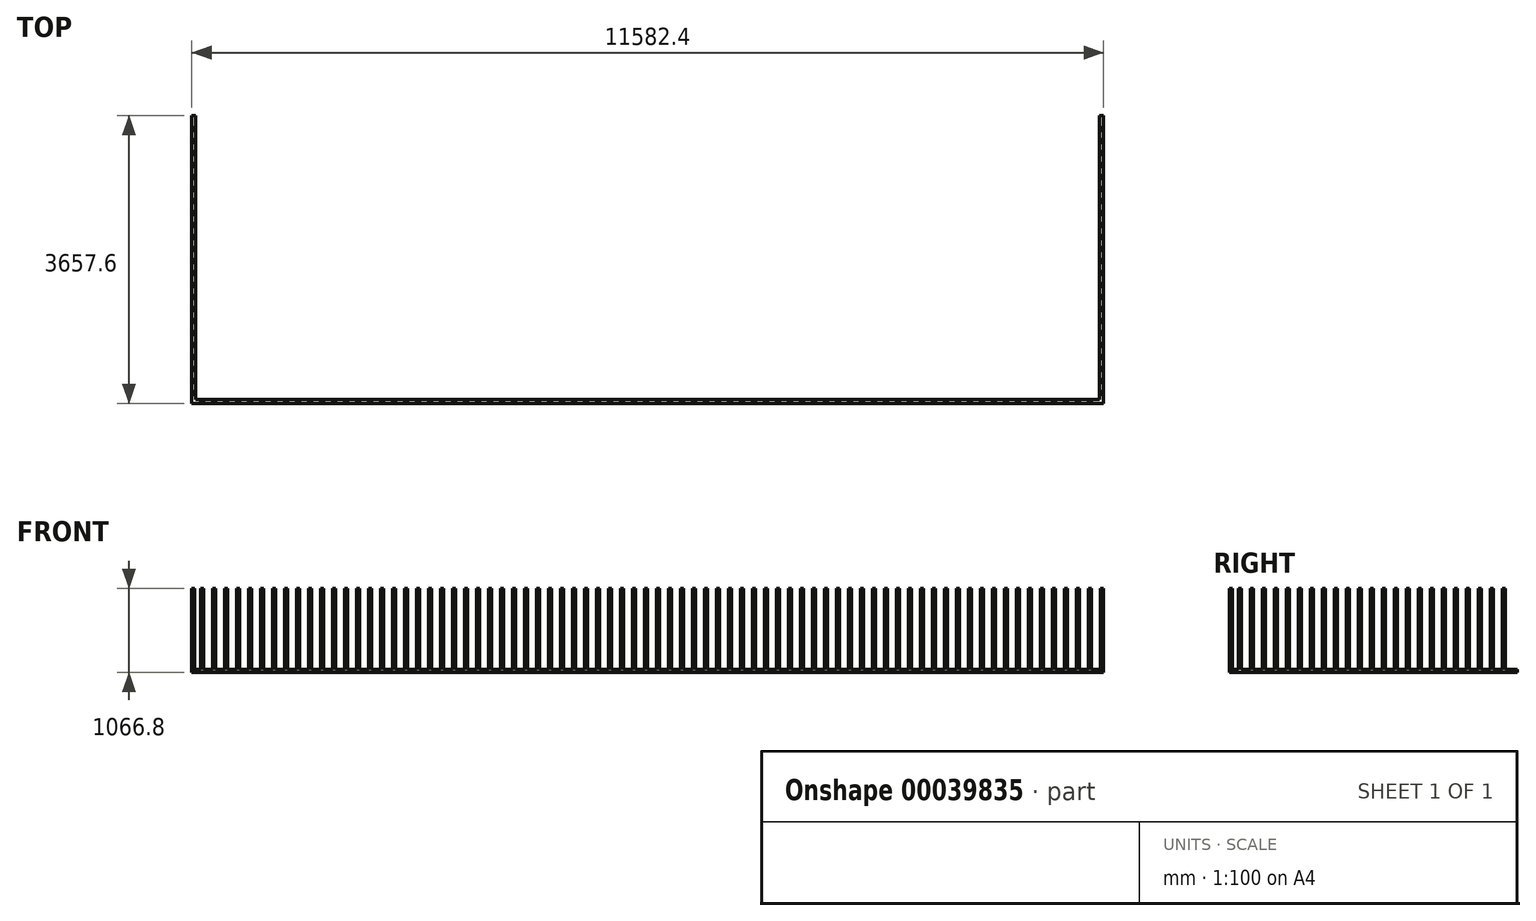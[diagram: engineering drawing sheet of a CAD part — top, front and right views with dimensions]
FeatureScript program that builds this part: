
annotation { "Feature Type Name" : "Feature", "Feature Type Description" : "" }
export const myFeature = defineFeature(function(context is Context, id is Id, definition is map)
    precondition{}
    {
        {
            var Q0;
            Q0=qCreatedBy(makeId("Top.planeOp"),FACE);
            var sketch = newSketch(context, id + "F0", { "sketchPlane" : qUnion([Q0])});
            skLineSegment(sketch, "E0", {"start": v(-11531.6, 0) * mm, "end": v(-11531.6, -3657.6) * mm});
            skLineSegment(sketch, "E1", {"start": v(-11531.6, -3657.6) * mm, "end": v(50.8, -3657.6) * mm});
            skLineSegment(sketch, "E2", {"start": v(50.8, -3657.6) * mm, "end": v(50.8, 0) * mm});
            skLineSegment(sketch, "E3", {"start": v(50.8, 0) * mm, "end": v(0, 0) * mm});
            skLineSegment(sketch, "E4", {"start": v(0, 0) * mm, "end": v(0, -3606.8) * mm});
            skLineSegment(sketch, "E5", {"start": v(0, -3606.8) * mm, "end": v(-11480.8, -3606.8) * mm});
            skLineSegment(sketch, "E6", {"start": v(-11480.8, -3606.8) * mm, "end": v(-11480.8, 0) * mm});
            skLineSegment(sketch, "E7", {"start": v(-11480.8, 0) * mm, "end": v(-11531.6, 0) * mm});
            skLineSegment(sketch, "E8.bottom", {"start": v(50.8, 0) * mm, "end": v(12.7, 0) * mm});
            skLineSegment(sketch, "E8.top", {"start": v(50.8, -38.1) * mm, "end": v(12.7, -38.1) * mm});
            skLineSegment(sketch, "E8.left", {"start": v(50.8, 0) * mm, "end": v(50.8, -38.1) * mm});
            skLineSegment(sketch, "E8.right", {"start": v(12.7, 0) * mm, "end": v(12.7, -38.1) * mm});
            skLineSegment(sketch, "E9.0.1.0", {"start": v(50.8, -190.5) * mm, "end": v(12.7, -190.5) * mm});
            skLineSegment(sketch, "E9.0.1.1", {"start": v(50.8, -152.4) * mm, "end": v(12.7, -152.4) * mm});
            skLineSegment(sketch, "E9.0.1.2", {"start": v(12.7, -152.4) * mm, "end": v(12.7, -190.5) * mm});
            skLineSegment(sketch, "E9.0.2.0", {"start": v(50.8, -342.9) * mm, "end": v(12.7, -342.9) * mm});
            skLineSegment(sketch, "E9.0.2.1", {"start": v(50.8, -304.8) * mm, "end": v(12.7, -304.8) * mm});
            skLineSegment(sketch, "E9.0.2.2", {"start": v(12.7, -304.8) * mm, "end": v(12.7, -342.9) * mm});
            skLineSegment(sketch, "E9.0.3.0", {"start": v(50.8, -495.3) * mm, "end": v(12.7, -495.3) * mm});
            skLineSegment(sketch, "E9.0.3.1", {"start": v(50.8, -457.2) * mm, "end": v(12.7, -457.2) * mm});
            skLineSegment(sketch, "E9.0.3.2", {"start": v(12.7, -457.2) * mm, "end": v(12.7, -495.3) * mm});
            skLineSegment(sketch, "E9.0.4.0", {"start": v(50.8, -647.7) * mm, "end": v(12.7, -647.7) * mm});
            skLineSegment(sketch, "E9.0.4.1", {"start": v(50.8, -609.6) * mm, "end": v(12.7, -609.6) * mm});
            skLineSegment(sketch, "E9.0.4.2", {"start": v(12.7, -609.6) * mm, "end": v(12.7, -647.7) * mm});
            skLineSegment(sketch, "E9.0.5.0", {"start": v(50.8, -800.1) * mm, "end": v(12.7, -800.1) * mm});
            skLineSegment(sketch, "E9.0.5.1", {"start": v(50.8, -762) * mm, "end": v(12.7, -762) * mm});
            skLineSegment(sketch, "E9.0.5.2", {"start": v(12.7, -762) * mm, "end": v(12.7, -800.1) * mm});
            skLineSegment(sketch, "E9.0.6.0", {"start": v(50.8, -952.5) * mm, "end": v(12.7, -952.5) * mm});
            skLineSegment(sketch, "E9.0.6.1", {"start": v(50.8, -914.4) * mm, "end": v(12.7, -914.4) * mm});
            skLineSegment(sketch, "E9.0.6.2", {"start": v(12.7, -914.4) * mm, "end": v(12.7, -952.5) * mm});
            skLineSegment(sketch, "E9.0.7.0", {"start": v(50.8, -1104.9) * mm, "end": v(12.7, -1104.9) * mm});
            skLineSegment(sketch, "E9.0.7.1", {"start": v(50.8, -1066.8) * mm, "end": v(12.7, -1066.8) * mm});
            skLineSegment(sketch, "E9.0.7.2", {"start": v(12.7, -1066.8) * mm, "end": v(12.7, -1104.9) * mm});
            skLineSegment(sketch, "E9.0.8.0", {"start": v(50.8, -1257.3) * mm, "end": v(12.7, -1257.3) * mm});
            skLineSegment(sketch, "E9.0.8.1", {"start": v(50.8, -1219.2) * mm, "end": v(12.7, -1219.2) * mm});
            skLineSegment(sketch, "E9.0.8.2", {"start": v(12.7, -1219.2) * mm, "end": v(12.7, -1257.3) * mm});
            skLineSegment(sketch, "E9.0.9.0", {"start": v(50.8, -1409.7) * mm, "end": v(12.7, -1409.7) * mm});
            skLineSegment(sketch, "E9.0.9.1", {"start": v(50.8, -1371.6) * mm, "end": v(12.7, -1371.6) * mm});
            skLineSegment(sketch, "E9.0.9.2", {"start": v(12.7, -1371.6) * mm, "end": v(12.7, -1409.7) * mm});
            skLineSegment(sketch, "E9.0.10.0", {"start": v(50.8, -1562.1) * mm, "end": v(12.7, -1562.1) * mm});
            skLineSegment(sketch, "E9.0.10.1", {"start": v(50.8, -1524) * mm, "end": v(12.7, -1524) * mm});
            skLineSegment(sketch, "E9.0.10.2", {"start": v(12.7, -1524) * mm, "end": v(12.7, -1562.1) * mm});
            skLineSegment(sketch, "E9.0.11.0", {"start": v(50.8, -1714.5) * mm, "end": v(12.7, -1714.5) * mm});
            skLineSegment(sketch, "E9.0.11.1", {"start": v(50.8, -1676.4) * mm, "end": v(12.7, -1676.4) * mm});
            skLineSegment(sketch, "E9.0.11.2", {"start": v(12.7, -1676.4) * mm, "end": v(12.7, -1714.5) * mm});
            skLineSegment(sketch, "E9.0.12.0", {"start": v(50.8, -1866.9) * mm, "end": v(12.7, -1866.9) * mm});
            skLineSegment(sketch, "E9.0.12.1", {"start": v(50.8, -1828.8) * mm, "end": v(12.7, -1828.8) * mm});
            skLineSegment(sketch, "E9.0.12.2", {"start": v(12.7, -1828.8) * mm, "end": v(12.7, -1866.9) * mm});
            skLineSegment(sketch, "E9.0.13.0", {"start": v(50.8, -2019.3) * mm, "end": v(12.7, -2019.3) * mm});
            skLineSegment(sketch, "E9.0.13.1", {"start": v(50.8, -1981.2) * mm, "end": v(12.7, -1981.2) * mm});
            skLineSegment(sketch, "E9.0.13.2", {"start": v(12.7, -1981.2) * mm, "end": v(12.7, -2019.3) * mm});
            skLineSegment(sketch, "E9.0.14.0", {"start": v(50.8, -2171.7) * mm, "end": v(12.7, -2171.7) * mm});
            skLineSegment(sketch, "E9.0.14.1", {"start": v(50.8, -2133.6) * mm, "end": v(12.7, -2133.6) * mm});
            skLineSegment(sketch, "E9.0.14.2", {"start": v(12.7, -2133.6) * mm, "end": v(12.7, -2171.7) * mm});
            skLineSegment(sketch, "E9.0.15.0", {"start": v(50.8, -2324.1) * mm, "end": v(12.7, -2324.1) * mm});
            skLineSegment(sketch, "E9.0.15.1", {"start": v(50.8, -2286) * mm, "end": v(12.7, -2286) * mm});
            skLineSegment(sketch, "E9.0.15.2", {"start": v(12.7, -2286) * mm, "end": v(12.7, -2324.1) * mm});
            skLineSegment(sketch, "E9.0.16.0", {"start": v(50.8, -2476.5) * mm, "end": v(12.7, -2476.5) * mm});
            skLineSegment(sketch, "E9.0.16.1", {"start": v(50.8, -2438.4) * mm, "end": v(12.7, -2438.4) * mm});
            skLineSegment(sketch, "E9.0.16.2", {"start": v(12.7, -2438.4) * mm, "end": v(12.7, -2476.5) * mm});
            skLineSegment(sketch, "E9.0.17.0", {"start": v(50.8, -2628.9) * mm, "end": v(12.7, -2628.9) * mm});
            skLineSegment(sketch, "E9.0.17.1", {"start": v(50.8, -2590.8) * mm, "end": v(12.7, -2590.8) * mm});
            skLineSegment(sketch, "E9.0.17.2", {"start": v(12.7, -2590.8) * mm, "end": v(12.7, -2628.9) * mm});
            skLineSegment(sketch, "E9.0.18.0", {"start": v(50.8, -2781.3) * mm, "end": v(12.7, -2781.3) * mm});
            skLineSegment(sketch, "E9.0.18.1", {"start": v(50.8, -2743.2) * mm, "end": v(12.7, -2743.2) * mm});
            skLineSegment(sketch, "E9.0.18.2", {"start": v(12.7, -2743.2) * mm, "end": v(12.7, -2781.3) * mm});
            skLineSegment(sketch, "E9.0.19.0", {"start": v(50.8, -2933.7) * mm, "end": v(12.7, -2933.7) * mm});
            skLineSegment(sketch, "E9.0.19.1", {"start": v(50.8, -2895.6) * mm, "end": v(12.7, -2895.6) * mm});
            skLineSegment(sketch, "E9.0.19.2", {"start": v(12.7, -2895.6) * mm, "end": v(12.7, -2933.7) * mm});
            skLineSegment(sketch, "E9.0.20.0", {"start": v(50.8, -3086.1) * mm, "end": v(12.7, -3086.1) * mm});
            skLineSegment(sketch, "E9.0.20.1", {"start": v(50.8, -3048) * mm, "end": v(12.7, -3048) * mm});
            skLineSegment(sketch, "E9.0.20.2", {"start": v(12.7, -3048) * mm, "end": v(12.7, -3086.1) * mm});
            skLineSegment(sketch, "E9.0.21.0", {"start": v(50.8, -3238.5) * mm, "end": v(12.7, -3238.5) * mm});
            skLineSegment(sketch, "E9.0.21.1", {"start": v(50.8, -3200.4) * mm, "end": v(12.7, -3200.4) * mm});
            skLineSegment(sketch, "E9.0.21.2", {"start": v(12.7, -3200.4) * mm, "end": v(12.7, -3238.5) * mm});
            skLineSegment(sketch, "E9.0.22.0", {"start": v(50.8, -3390.9) * mm, "end": v(12.7, -3390.9) * mm});
            skLineSegment(sketch, "E9.0.22.1", {"start": v(50.8, -3352.8) * mm, "end": v(12.7, -3352.8) * mm});
            skLineSegment(sketch, "E9.0.22.2", {"start": v(12.7, -3352.8) * mm, "end": v(12.7, -3390.9) * mm});
            skLineSegment(sketch, "E9.0.23.0", {"start": v(50.8, -3543.3) * mm, "end": v(12.7, -3543.3) * mm});
            skLineSegment(sketch, "E9.0.23.1", {"start": v(50.8, -3505.2) * mm, "end": v(12.7, -3505.2) * mm});
            skLineSegment(sketch, "E9.0.23.2", {"start": v(12.7, -3505.2) * mm, "end": v(12.7, -3543.3) * mm});
            skLineSegment(sketch, "E9.direction1", {"start": v(12.7, -38.1) * mm, "end": v(-12.7, -38.1) * mm, "construction": true});
            skLineSegment(sketch, "E9.direction2", {"start": v(12.7, -38.1) * mm, "end": v(12.7, -190.5) * mm, "construction": true});
            skLineSegment(sketch, "E10.bottom", {"start": v(50.8, -3657.6) * mm, "end": v(12.7, -3657.6) * mm});
            skLineSegment(sketch, "E10.top", {"start": v(50.8, -3619.5) * mm, "end": v(12.7, -3619.5) * mm});
            skLineSegment(sketch, "E10.left", {"start": v(50.8, -3657.6) * mm, "end": v(50.8, -3619.5) * mm});
            skLineSegment(sketch, "E10.right", {"start": v(12.7, -3657.6) * mm, "end": v(12.7, -3619.5) * mm});
            skLineSegment(sketch, "E11.1.0.0", {"start": v(-139.7, -3657.6) * mm, "end": v(-139.7, -3619.5) * mm});
            skLineSegment(sketch, "E11.1.0.1", {"start": v(-101.6, -3657.6) * mm, "end": v(-101.6, -3619.5) * mm});
            skLineSegment(sketch, "E11.1.0.2", {"start": v(-101.6, -3619.5) * mm, "end": v(-139.7, -3619.5) * mm});
            skLineSegment(sketch, "E11.1.0.3", {"start": v(-101.6, -3657.6) * mm, "end": v(-139.7, -3657.6) * mm});
            skLineSegment(sketch, "E11.2.0.0", {"start": v(-292.1, -3657.6) * mm, "end": v(-292.1, -3619.5) * mm});
            skLineSegment(sketch, "E11.2.0.1", {"start": v(-254, -3657.6) * mm, "end": v(-254, -3619.5) * mm});
            skLineSegment(sketch, "E11.2.0.2", {"start": v(-254, -3619.5) * mm, "end": v(-292.1, -3619.5) * mm});
            skLineSegment(sketch, "E11.2.0.3", {"start": v(-254, -3657.6) * mm, "end": v(-292.1, -3657.6) * mm});
            skLineSegment(sketch, "E11.3.0.0", {"start": v(-444.5, -3657.6) * mm, "end": v(-444.5, -3619.5) * mm});
            skLineSegment(sketch, "E11.3.0.1", {"start": v(-406.4, -3657.6) * mm, "end": v(-406.4, -3619.5) * mm});
            skLineSegment(sketch, "E11.3.0.2", {"start": v(-406.4, -3619.5) * mm, "end": v(-444.5, -3619.5) * mm});
            skLineSegment(sketch, "E11.3.0.3", {"start": v(-406.4, -3657.6) * mm, "end": v(-444.5, -3657.6) * mm});
            skLineSegment(sketch, "E11.4.0.0", {"start": v(-596.9, -3657.6) * mm, "end": v(-596.9, -3619.5) * mm});
            skLineSegment(sketch, "E11.4.0.1", {"start": v(-558.8, -3657.6) * mm, "end": v(-558.8, -3619.5) * mm});
            skLineSegment(sketch, "E11.4.0.2", {"start": v(-558.8, -3619.5) * mm, "end": v(-596.9, -3619.5) * mm});
            skLineSegment(sketch, "E11.4.0.3", {"start": v(-558.8, -3657.6) * mm, "end": v(-596.9, -3657.6) * mm});
            skLineSegment(sketch, "E11.5.0.0", {"start": v(-749.3, -3657.6) * mm, "end": v(-749.3, -3619.5) * mm});
            skLineSegment(sketch, "E11.5.0.1", {"start": v(-711.2, -3657.6) * mm, "end": v(-711.2, -3619.5) * mm});
            skLineSegment(sketch, "E11.5.0.2", {"start": v(-711.2, -3619.5) * mm, "end": v(-749.3, -3619.5) * mm});
            skLineSegment(sketch, "E11.5.0.3", {"start": v(-711.2, -3657.6) * mm, "end": v(-749.3, -3657.6) * mm});
            skLineSegment(sketch, "E11.6.0.0", {"start": v(-901.7, -3657.6) * mm, "end": v(-901.7, -3619.5) * mm});
            skLineSegment(sketch, "E11.6.0.1", {"start": v(-863.6, -3657.6) * mm, "end": v(-863.6, -3619.5) * mm});
            skLineSegment(sketch, "E11.6.0.2", {"start": v(-863.6, -3619.5) * mm, "end": v(-901.7, -3619.5) * mm});
            skLineSegment(sketch, "E11.6.0.3", {"start": v(-863.6, -3657.6) * mm, "end": v(-901.7, -3657.6) * mm});
            skLineSegment(sketch, "E11.7.0.0", {"start": v(-1054.1, -3657.6) * mm, "end": v(-1054.1, -3619.5) * mm});
            skLineSegment(sketch, "E11.7.0.1", {"start": v(-1016, -3657.6) * mm, "end": v(-1016, -3619.5) * mm});
            skLineSegment(sketch, "E11.7.0.2", {"start": v(-1016, -3619.5) * mm, "end": v(-1054.1, -3619.5) * mm});
            skLineSegment(sketch, "E11.7.0.3", {"start": v(-1016, -3657.6) * mm, "end": v(-1054.1, -3657.6) * mm});
            skLineSegment(sketch, "E11.8.0.0", {"start": v(-1206.5, -3657.6) * mm, "end": v(-1206.5, -3619.5) * mm});
            skLineSegment(sketch, "E11.8.0.1", {"start": v(-1168.4, -3657.6) * mm, "end": v(-1168.4, -3619.5) * mm});
            skLineSegment(sketch, "E11.8.0.2", {"start": v(-1168.4, -3619.5) * mm, "end": v(-1206.5, -3619.5) * mm});
            skLineSegment(sketch, "E11.8.0.3", {"start": v(-1168.4, -3657.6) * mm, "end": v(-1206.5, -3657.6) * mm});
            skLineSegment(sketch, "E11.9.0.0", {"start": v(-1358.9, -3657.6) * mm, "end": v(-1358.9, -3619.5) * mm});
            skLineSegment(sketch, "E11.9.0.1", {"start": v(-1320.8, -3657.6) * mm, "end": v(-1320.8, -3619.5) * mm});
            skLineSegment(sketch, "E11.9.0.2", {"start": v(-1320.8, -3619.5) * mm, "end": v(-1358.9, -3619.5) * mm});
            skLineSegment(sketch, "E11.9.0.3", {"start": v(-1320.8, -3657.6) * mm, "end": v(-1358.9, -3657.6) * mm});
            skLineSegment(sketch, "E11.10.0.0", {"start": v(-1511.3, -3657.6) * mm, "end": v(-1511.3, -3619.5) * mm});
            skLineSegment(sketch, "E11.10.0.1", {"start": v(-1473.2, -3657.6) * mm, "end": v(-1473.2, -3619.5) * mm});
            skLineSegment(sketch, "E11.10.0.2", {"start": v(-1473.2, -3619.5) * mm, "end": v(-1511.3, -3619.5) * mm});
            skLineSegment(sketch, "E11.10.0.3", {"start": v(-1473.2, -3657.6) * mm, "end": v(-1511.3, -3657.6) * mm});
            skLineSegment(sketch, "E11.11.0.0", {"start": v(-1663.7, -3657.6) * mm, "end": v(-1663.7, -3619.5) * mm});
            skLineSegment(sketch, "E11.11.0.1", {"start": v(-1625.6, -3657.6) * mm, "end": v(-1625.6, -3619.5) * mm});
            skLineSegment(sketch, "E11.11.0.2", {"start": v(-1625.6, -3619.5) * mm, "end": v(-1663.7, -3619.5) * mm});
            skLineSegment(sketch, "E11.11.0.3", {"start": v(-1625.6, -3657.6) * mm, "end": v(-1663.7, -3657.6) * mm});
            skLineSegment(sketch, "E11.12.0.0", {"start": v(-1816.1, -3657.6) * mm, "end": v(-1816.1, -3619.5) * mm});
            skLineSegment(sketch, "E11.12.0.1", {"start": v(-1778, -3657.6) * mm, "end": v(-1778, -3619.5) * mm});
            skLineSegment(sketch, "E11.12.0.2", {"start": v(-1778, -3619.5) * mm, "end": v(-1816.1, -3619.5) * mm});
            skLineSegment(sketch, "E11.12.0.3", {"start": v(-1778, -3657.6) * mm, "end": v(-1816.1, -3657.6) * mm});
            skLineSegment(sketch, "E11.13.0.0", {"start": v(-1968.5, -3657.6) * mm, "end": v(-1968.5, -3619.5) * mm});
            skLineSegment(sketch, "E11.13.0.1", {"start": v(-1930.4, -3657.6) * mm, "end": v(-1930.4, -3619.5) * mm});
            skLineSegment(sketch, "E11.13.0.2", {"start": v(-1930.4, -3619.5) * mm, "end": v(-1968.5, -3619.5) * mm});
            skLineSegment(sketch, "E11.13.0.3", {"start": v(-1930.4, -3657.6) * mm, "end": v(-1968.5, -3657.6) * mm});
            skLineSegment(sketch, "E11.14.0.0", {"start": v(-2120.9, -3657.6) * mm, "end": v(-2120.9, -3619.5) * mm});
            skLineSegment(sketch, "E11.14.0.1", {"start": v(-2082.8, -3657.6) * mm, "end": v(-2082.8, -3619.5) * mm});
            skLineSegment(sketch, "E11.14.0.2", {"start": v(-2082.8, -3619.5) * mm, "end": v(-2120.9, -3619.5) * mm});
            skLineSegment(sketch, "E11.14.0.3", {"start": v(-2082.8, -3657.6) * mm, "end": v(-2120.9, -3657.6) * mm});
            skLineSegment(sketch, "E11.15.0.0", {"start": v(-2273.3, -3657.6) * mm, "end": v(-2273.3, -3619.5) * mm});
            skLineSegment(sketch, "E11.15.0.1", {"start": v(-2235.2, -3657.6) * mm, "end": v(-2235.2, -3619.5) * mm});
            skLineSegment(sketch, "E11.15.0.2", {"start": v(-2235.2, -3619.5) * mm, "end": v(-2273.3, -3619.5) * mm});
            skLineSegment(sketch, "E11.15.0.3", {"start": v(-2235.2, -3657.6) * mm, "end": v(-2273.3, -3657.6) * mm});
            skLineSegment(sketch, "E11.16.0.0", {"start": v(-2425.7, -3657.6) * mm, "end": v(-2425.7, -3619.5) * mm});
            skLineSegment(sketch, "E11.16.0.1", {"start": v(-2387.6, -3657.6) * mm, "end": v(-2387.6, -3619.5) * mm});
            skLineSegment(sketch, "E11.16.0.2", {"start": v(-2387.6, -3619.5) * mm, "end": v(-2425.7, -3619.5) * mm});
            skLineSegment(sketch, "E11.16.0.3", {"start": v(-2387.6, -3657.6) * mm, "end": v(-2425.7, -3657.6) * mm});
            skLineSegment(sketch, "E11.17.0.0", {"start": v(-2578.1, -3657.6) * mm, "end": v(-2578.1, -3619.5) * mm});
            skLineSegment(sketch, "E11.17.0.1", {"start": v(-2540, -3657.6) * mm, "end": v(-2540, -3619.5) * mm});
            skLineSegment(sketch, "E11.17.0.2", {"start": v(-2540, -3619.5) * mm, "end": v(-2578.1, -3619.5) * mm});
            skLineSegment(sketch, "E11.17.0.3", {"start": v(-2540, -3657.6) * mm, "end": v(-2578.1, -3657.6) * mm});
            skLineSegment(sketch, "E11.18.0.0", {"start": v(-2730.5, -3657.6) * mm, "end": v(-2730.5, -3619.5) * mm});
            skLineSegment(sketch, "E11.18.0.1", {"start": v(-2692.4, -3657.6) * mm, "end": v(-2692.4, -3619.5) * mm});
            skLineSegment(sketch, "E11.18.0.2", {"start": v(-2692.4, -3619.5) * mm, "end": v(-2730.5, -3619.5) * mm});
            skLineSegment(sketch, "E11.18.0.3", {"start": v(-2692.4, -3657.6) * mm, "end": v(-2730.5, -3657.6) * mm});
            skLineSegment(sketch, "E11.19.0.0", {"start": v(-2882.9, -3657.6) * mm, "end": v(-2882.9, -3619.5) * mm});
            skLineSegment(sketch, "E11.19.0.1", {"start": v(-2844.8, -3657.6) * mm, "end": v(-2844.8, -3619.5) * mm});
            skLineSegment(sketch, "E11.19.0.2", {"start": v(-2844.8, -3619.5) * mm, "end": v(-2882.9, -3619.5) * mm});
            skLineSegment(sketch, "E11.19.0.3", {"start": v(-2844.8, -3657.6) * mm, "end": v(-2882.9, -3657.6) * mm});
            skLineSegment(sketch, "E11.20.0.0", {"start": v(-3035.3, -3657.6) * mm, "end": v(-3035.3, -3619.5) * mm});
            skLineSegment(sketch, "E11.20.0.1", {"start": v(-2997.2, -3657.6) * mm, "end": v(-2997.2, -3619.5) * mm});
            skLineSegment(sketch, "E11.20.0.2", {"start": v(-2997.2, -3619.5) * mm, "end": v(-3035.3, -3619.5) * mm});
            skLineSegment(sketch, "E11.20.0.3", {"start": v(-2997.2, -3657.6) * mm, "end": v(-3035.3, -3657.6) * mm});
            skLineSegment(sketch, "E11.21.0.0", {"start": v(-3187.7, -3657.6) * mm, "end": v(-3187.7, -3619.5) * mm});
            skLineSegment(sketch, "E11.21.0.1", {"start": v(-3149.6, -3657.6) * mm, "end": v(-3149.6, -3619.5) * mm});
            skLineSegment(sketch, "E11.21.0.2", {"start": v(-3149.6, -3619.5) * mm, "end": v(-3187.7, -3619.5) * mm});
            skLineSegment(sketch, "E11.21.0.3", {"start": v(-3149.6, -3657.6) * mm, "end": v(-3187.7, -3657.6) * mm});
            skLineSegment(sketch, "E11.22.0.0", {"start": v(-3340.1, -3657.6) * mm, "end": v(-3340.1, -3619.5) * mm});
            skLineSegment(sketch, "E11.22.0.1", {"start": v(-3302, -3657.6) * mm, "end": v(-3302, -3619.5) * mm});
            skLineSegment(sketch, "E11.22.0.2", {"start": v(-3302, -3619.5) * mm, "end": v(-3340.1, -3619.5) * mm});
            skLineSegment(sketch, "E11.22.0.3", {"start": v(-3302, -3657.6) * mm, "end": v(-3340.1, -3657.6) * mm});
            skLineSegment(sketch, "E11.23.0.0", {"start": v(-3492.5, -3657.6) * mm, "end": v(-3492.5, -3619.5) * mm});
            skLineSegment(sketch, "E11.23.0.1", {"start": v(-3454.4, -3657.6) * mm, "end": v(-3454.4, -3619.5) * mm});
            skLineSegment(sketch, "E11.23.0.2", {"start": v(-3454.4, -3619.5) * mm, "end": v(-3492.5, -3619.5) * mm});
            skLineSegment(sketch, "E11.23.0.3", {"start": v(-3454.4, -3657.6) * mm, "end": v(-3492.5, -3657.6) * mm});
            skLineSegment(sketch, "E11.24.0.0", {"start": v(-3644.9, -3657.6) * mm, "end": v(-3644.9, -3619.5) * mm});
            skLineSegment(sketch, "E11.24.0.1", {"start": v(-3606.8, -3657.6) * mm, "end": v(-3606.8, -3619.5) * mm});
            skLineSegment(sketch, "E11.24.0.2", {"start": v(-3606.8, -3619.5) * mm, "end": v(-3644.9, -3619.5) * mm});
            skLineSegment(sketch, "E11.24.0.3", {"start": v(-3606.8, -3657.6) * mm, "end": v(-3644.9, -3657.6) * mm});
            skLineSegment(sketch, "E11.25.0.0", {"start": v(-3797.3, -3657.6) * mm, "end": v(-3797.3, -3619.5) * mm});
            skLineSegment(sketch, "E11.25.0.1", {"start": v(-3759.2, -3657.6) * mm, "end": v(-3759.2, -3619.5) * mm});
            skLineSegment(sketch, "E11.25.0.2", {"start": v(-3759.2, -3619.5) * mm, "end": v(-3797.3, -3619.5) * mm});
            skLineSegment(sketch, "E11.25.0.3", {"start": v(-3759.2, -3657.6) * mm, "end": v(-3797.3, -3657.6) * mm});
            skLineSegment(sketch, "E11.26.0.0", {"start": v(-3949.7, -3657.6) * mm, "end": v(-3949.7, -3619.5) * mm});
            skLineSegment(sketch, "E11.26.0.1", {"start": v(-3911.6, -3657.6) * mm, "end": v(-3911.6, -3619.5) * mm});
            skLineSegment(sketch, "E11.26.0.2", {"start": v(-3911.6, -3619.5) * mm, "end": v(-3949.7, -3619.5) * mm});
            skLineSegment(sketch, "E11.26.0.3", {"start": v(-3911.6, -3657.6) * mm, "end": v(-3949.7, -3657.6) * mm});
            skLineSegment(sketch, "E11.27.0.0", {"start": v(-4102.1, -3657.6) * mm, "end": v(-4102.1, -3619.5) * mm});
            skLineSegment(sketch, "E11.27.0.1", {"start": v(-4064, -3657.6) * mm, "end": v(-4064, -3619.5) * mm});
            skLineSegment(sketch, "E11.27.0.2", {"start": v(-4064, -3619.5) * mm, "end": v(-4102.1, -3619.5) * mm});
            skLineSegment(sketch, "E11.27.0.3", {"start": v(-4064, -3657.6) * mm, "end": v(-4102.1, -3657.6) * mm});
            skLineSegment(sketch, "E11.28.0.0", {"start": v(-4254.5, -3657.6) * mm, "end": v(-4254.5, -3619.5) * mm});
            skLineSegment(sketch, "E11.28.0.1", {"start": v(-4216.4, -3657.6) * mm, "end": v(-4216.4, -3619.5) * mm});
            skLineSegment(sketch, "E11.28.0.2", {"start": v(-4216.4, -3619.5) * mm, "end": v(-4254.5, -3619.5) * mm});
            skLineSegment(sketch, "E11.28.0.3", {"start": v(-4216.4, -3657.6) * mm, "end": v(-4254.5, -3657.6) * mm});
            skLineSegment(sketch, "E11.29.0.0", {"start": v(-4406.9, -3657.6) * mm, "end": v(-4406.9, -3619.5) * mm});
            skLineSegment(sketch, "E11.29.0.1", {"start": v(-4368.8, -3657.6) * mm, "end": v(-4368.8, -3619.5) * mm});
            skLineSegment(sketch, "E11.29.0.2", {"start": v(-4368.8, -3619.5) * mm, "end": v(-4406.9, -3619.5) * mm});
            skLineSegment(sketch, "E11.29.0.3", {"start": v(-4368.8, -3657.6) * mm, "end": v(-4406.9, -3657.6) * mm});
            skLineSegment(sketch, "E11.30.0.0", {"start": v(-4559.3, -3657.6) * mm, "end": v(-4559.3, -3619.5) * mm});
            skLineSegment(sketch, "E11.30.0.1", {"start": v(-4521.2, -3657.6) * mm, "end": v(-4521.2, -3619.5) * mm});
            skLineSegment(sketch, "E11.30.0.2", {"start": v(-4521.2, -3619.5) * mm, "end": v(-4559.3, -3619.5) * mm});
            skLineSegment(sketch, "E11.30.0.3", {"start": v(-4521.2, -3657.6) * mm, "end": v(-4559.3, -3657.6) * mm});
            skLineSegment(sketch, "E11.31.0.0", {"start": v(-4711.7, -3657.6) * mm, "end": v(-4711.7, -3619.5) * mm});
            skLineSegment(sketch, "E11.31.0.1", {"start": v(-4673.6, -3657.6) * mm, "end": v(-4673.6, -3619.5) * mm});
            skLineSegment(sketch, "E11.31.0.2", {"start": v(-4673.6, -3619.5) * mm, "end": v(-4711.7, -3619.5) * mm});
            skLineSegment(sketch, "E11.31.0.3", {"start": v(-4673.6, -3657.6) * mm, "end": v(-4711.7, -3657.6) * mm});
            skLineSegment(sketch, "E11.32.0.0", {"start": v(-4864.1, -3657.6) * mm, "end": v(-4864.1, -3619.5) * mm});
            skLineSegment(sketch, "E11.32.0.1", {"start": v(-4826, -3657.6) * mm, "end": v(-4826, -3619.5) * mm});
            skLineSegment(sketch, "E11.32.0.2", {"start": v(-4826, -3619.5) * mm, "end": v(-4864.1, -3619.5) * mm});
            skLineSegment(sketch, "E11.32.0.3", {"start": v(-4826, -3657.6) * mm, "end": v(-4864.1, -3657.6) * mm});
            skLineSegment(sketch, "E11.33.0.0", {"start": v(-5016.5, -3657.6) * mm, "end": v(-5016.5, -3619.5) * mm});
            skLineSegment(sketch, "E11.33.0.1", {"start": v(-4978.4, -3657.6) * mm, "end": v(-4978.4, -3619.5) * mm});
            skLineSegment(sketch, "E11.33.0.2", {"start": v(-4978.4, -3619.5) * mm, "end": v(-5016.5, -3619.5) * mm});
            skLineSegment(sketch, "E11.33.0.3", {"start": v(-4978.4, -3657.6) * mm, "end": v(-5016.5, -3657.6) * mm});
            skLineSegment(sketch, "E11.34.0.0", {"start": v(-5168.9, -3657.6) * mm, "end": v(-5168.9, -3619.5) * mm});
            skLineSegment(sketch, "E11.34.0.1", {"start": v(-5130.8, -3657.6) * mm, "end": v(-5130.8, -3619.5) * mm});
            skLineSegment(sketch, "E11.34.0.2", {"start": v(-5130.8, -3619.5) * mm, "end": v(-5168.9, -3619.5) * mm});
            skLineSegment(sketch, "E11.34.0.3", {"start": v(-5130.8, -3657.6) * mm, "end": v(-5168.9, -3657.6) * mm});
            skLineSegment(sketch, "E11.35.0.0", {"start": v(-5321.3, -3657.6) * mm, "end": v(-5321.3, -3619.5) * mm});
            skLineSegment(sketch, "E11.35.0.1", {"start": v(-5283.2, -3657.6) * mm, "end": v(-5283.2, -3619.5) * mm});
            skLineSegment(sketch, "E11.35.0.2", {"start": v(-5283.2, -3619.5) * mm, "end": v(-5321.3, -3619.5) * mm});
            skLineSegment(sketch, "E11.35.0.3", {"start": v(-5283.2, -3657.6) * mm, "end": v(-5321.3, -3657.6) * mm});
            skLineSegment(sketch, "E11.36.0.0", {"start": v(-5473.7, -3657.6) * mm, "end": v(-5473.7, -3619.5) * mm});
            skLineSegment(sketch, "E11.36.0.1", {"start": v(-5435.6, -3657.6) * mm, "end": v(-5435.6, -3619.5) * mm});
            skLineSegment(sketch, "E11.36.0.2", {"start": v(-5435.6, -3619.5) * mm, "end": v(-5473.7, -3619.5) * mm});
            skLineSegment(sketch, "E11.36.0.3", {"start": v(-5435.6, -3657.6) * mm, "end": v(-5473.7, -3657.6) * mm});
            skLineSegment(sketch, "E11.37.0.0", {"start": v(-5626.1, -3657.6) * mm, "end": v(-5626.1, -3619.5) * mm});
            skLineSegment(sketch, "E11.37.0.1", {"start": v(-5588, -3657.6) * mm, "end": v(-5588, -3619.5) * mm});
            skLineSegment(sketch, "E11.37.0.2", {"start": v(-5588, -3619.5) * mm, "end": v(-5626.1, -3619.5) * mm});
            skLineSegment(sketch, "E11.37.0.3", {"start": v(-5588, -3657.6) * mm, "end": v(-5626.1, -3657.6) * mm});
            skLineSegment(sketch, "E11.38.0.0", {"start": v(-5778.5, -3657.6) * mm, "end": v(-5778.5, -3619.5) * mm});
            skLineSegment(sketch, "E11.38.0.1", {"start": v(-5740.4, -3657.6) * mm, "end": v(-5740.4, -3619.5) * mm});
            skLineSegment(sketch, "E11.38.0.2", {"start": v(-5740.4, -3619.5) * mm, "end": v(-5778.5, -3619.5) * mm});
            skLineSegment(sketch, "E11.38.0.3", {"start": v(-5740.4, -3657.6) * mm, "end": v(-5778.5, -3657.6) * mm});
            skLineSegment(sketch, "E11.39.0.0", {"start": v(-5930.9, -3657.6) * mm, "end": v(-5930.9, -3619.5) * mm});
            skLineSegment(sketch, "E11.39.0.1", {"start": v(-5892.8, -3657.6) * mm, "end": v(-5892.8, -3619.5) * mm});
            skLineSegment(sketch, "E11.39.0.2", {"start": v(-5892.8, -3619.5) * mm, "end": v(-5930.9, -3619.5) * mm});
            skLineSegment(sketch, "E11.39.0.3", {"start": v(-5892.8, -3657.6) * mm, "end": v(-5930.9, -3657.6) * mm});
            skLineSegment(sketch, "E11.40.0.0", {"start": v(-6083.3, -3657.6) * mm, "end": v(-6083.3, -3619.5) * mm});
            skLineSegment(sketch, "E11.40.0.1", {"start": v(-6045.2, -3657.6) * mm, "end": v(-6045.2, -3619.5) * mm});
            skLineSegment(sketch, "E11.40.0.2", {"start": v(-6045.2, -3619.5) * mm, "end": v(-6083.3, -3619.5) * mm});
            skLineSegment(sketch, "E11.40.0.3", {"start": v(-6045.2, -3657.6) * mm, "end": v(-6083.3, -3657.6) * mm});
            skLineSegment(sketch, "E11.41.0.0", {"start": v(-6235.7, -3657.6) * mm, "end": v(-6235.7, -3619.5) * mm});
            skLineSegment(sketch, "E11.41.0.1", {"start": v(-6197.6, -3657.6) * mm, "end": v(-6197.6, -3619.5) * mm});
            skLineSegment(sketch, "E11.41.0.2", {"start": v(-6197.6, -3619.5) * mm, "end": v(-6235.7, -3619.5) * mm});
            skLineSegment(sketch, "E11.41.0.3", {"start": v(-6197.6, -3657.6) * mm, "end": v(-6235.7, -3657.6) * mm});
            skLineSegment(sketch, "E11.42.0.0", {"start": v(-6388.1, -3657.6) * mm, "end": v(-6388.1, -3619.5) * mm});
            skLineSegment(sketch, "E11.42.0.1", {"start": v(-6350, -3657.6) * mm, "end": v(-6350, -3619.5) * mm});
            skLineSegment(sketch, "E11.42.0.2", {"start": v(-6350, -3619.5) * mm, "end": v(-6388.1, -3619.5) * mm});
            skLineSegment(sketch, "E11.42.0.3", {"start": v(-6350, -3657.6) * mm, "end": v(-6388.1, -3657.6) * mm});
            skLineSegment(sketch, "E11.43.0.0", {"start": v(-6540.5, -3657.6) * mm, "end": v(-6540.5, -3619.5) * mm});
            skLineSegment(sketch, "E11.43.0.1", {"start": v(-6502.4, -3657.6) * mm, "end": v(-6502.4, -3619.5) * mm});
            skLineSegment(sketch, "E11.43.0.2", {"start": v(-6502.4, -3619.5) * mm, "end": v(-6540.5, -3619.5) * mm});
            skLineSegment(sketch, "E11.43.0.3", {"start": v(-6502.4, -3657.6) * mm, "end": v(-6540.5, -3657.6) * mm});
            skLineSegment(sketch, "E11.44.0.0", {"start": v(-6692.9, -3657.6) * mm, "end": v(-6692.9, -3619.5) * mm});
            skLineSegment(sketch, "E11.44.0.1", {"start": v(-6654.8, -3657.6) * mm, "end": v(-6654.8, -3619.5) * mm});
            skLineSegment(sketch, "E11.44.0.2", {"start": v(-6654.8, -3619.5) * mm, "end": v(-6692.9, -3619.5) * mm});
            skLineSegment(sketch, "E11.44.0.3", {"start": v(-6654.8, -3657.6) * mm, "end": v(-6692.9, -3657.6) * mm});
            skLineSegment(sketch, "E11.45.0.0", {"start": v(-6845.3, -3657.6) * mm, "end": v(-6845.3, -3619.5) * mm});
            skLineSegment(sketch, "E11.45.0.1", {"start": v(-6807.2, -3657.6) * mm, "end": v(-6807.2, -3619.5) * mm});
            skLineSegment(sketch, "E11.45.0.2", {"start": v(-6807.2, -3619.5) * mm, "end": v(-6845.3, -3619.5) * mm});
            skLineSegment(sketch, "E11.45.0.3", {"start": v(-6807.2, -3657.6) * mm, "end": v(-6845.3, -3657.6) * mm});
            skLineSegment(sketch, "E11.46.0.0", {"start": v(-6997.7, -3657.6) * mm, "end": v(-6997.7, -3619.5) * mm});
            skLineSegment(sketch, "E11.46.0.1", {"start": v(-6959.6, -3657.6) * mm, "end": v(-6959.6, -3619.5) * mm});
            skLineSegment(sketch, "E11.46.0.2", {"start": v(-6959.6, -3619.5) * mm, "end": v(-6997.7, -3619.5) * mm});
            skLineSegment(sketch, "E11.46.0.3", {"start": v(-6959.6, -3657.6) * mm, "end": v(-6997.7, -3657.6) * mm});
            skLineSegment(sketch, "E11.47.0.0", {"start": v(-7150.1, -3657.6) * mm, "end": v(-7150.1, -3619.5) * mm});
            skLineSegment(sketch, "E11.47.0.1", {"start": v(-7112, -3657.6) * mm, "end": v(-7112, -3619.5) * mm});
            skLineSegment(sketch, "E11.47.0.2", {"start": v(-7112, -3619.5) * mm, "end": v(-7150.1, -3619.5) * mm});
            skLineSegment(sketch, "E11.47.0.3", {"start": v(-7112, -3657.6) * mm, "end": v(-7150.1, -3657.6) * mm});
            skLineSegment(sketch, "E11.48.0.0", {"start": v(-7302.5, -3657.6) * mm, "end": v(-7302.5, -3619.5) * mm});
            skLineSegment(sketch, "E11.48.0.1", {"start": v(-7264.4, -3657.6) * mm, "end": v(-7264.4, -3619.5) * mm});
            skLineSegment(sketch, "E11.48.0.2", {"start": v(-7264.4, -3619.5) * mm, "end": v(-7302.5, -3619.5) * mm});
            skLineSegment(sketch, "E11.48.0.3", {"start": v(-7264.4, -3657.6) * mm, "end": v(-7302.5, -3657.6) * mm});
            skLineSegment(sketch, "E11.49.0.0", {"start": v(-7454.9, -3657.6) * mm, "end": v(-7454.9, -3619.5) * mm});
            skLineSegment(sketch, "E11.49.0.1", {"start": v(-7416.8, -3657.6) * mm, "end": v(-7416.8, -3619.5) * mm});
            skLineSegment(sketch, "E11.49.0.2", {"start": v(-7416.8, -3619.5) * mm, "end": v(-7454.9, -3619.5) * mm});
            skLineSegment(sketch, "E11.49.0.3", {"start": v(-7416.8, -3657.6) * mm, "end": v(-7454.9, -3657.6) * mm});
            skLineSegment(sketch, "E11.50.0.0", {"start": v(-7607.3, -3657.6) * mm, "end": v(-7607.3, -3619.5) * mm});
            skLineSegment(sketch, "E11.50.0.1", {"start": v(-7569.2, -3657.6) * mm, "end": v(-7569.2, -3619.5) * mm});
            skLineSegment(sketch, "E11.50.0.2", {"start": v(-7569.2, -3619.5) * mm, "end": v(-7607.3, -3619.5) * mm});
            skLineSegment(sketch, "E11.50.0.3", {"start": v(-7569.2, -3657.6) * mm, "end": v(-7607.3, -3657.6) * mm});
            skLineSegment(sketch, "E11.51.0.0", {"start": v(-7759.7, -3657.6) * mm, "end": v(-7759.7, -3619.5) * mm});
            skLineSegment(sketch, "E11.51.0.1", {"start": v(-7721.6, -3657.6) * mm, "end": v(-7721.6, -3619.5) * mm});
            skLineSegment(sketch, "E11.51.0.2", {"start": v(-7721.6, -3619.5) * mm, "end": v(-7759.7, -3619.5) * mm});
            skLineSegment(sketch, "E11.51.0.3", {"start": v(-7721.6, -3657.6) * mm, "end": v(-7759.7, -3657.6) * mm});
            skLineSegment(sketch, "E11.52.0.0", {"start": v(-7912.1, -3657.6) * mm, "end": v(-7912.1, -3619.5) * mm});
            skLineSegment(sketch, "E11.52.0.1", {"start": v(-7874, -3657.6) * mm, "end": v(-7874, -3619.5) * mm});
            skLineSegment(sketch, "E11.52.0.2", {"start": v(-7874, -3619.5) * mm, "end": v(-7912.1, -3619.5) * mm});
            skLineSegment(sketch, "E11.52.0.3", {"start": v(-7874, -3657.6) * mm, "end": v(-7912.1, -3657.6) * mm});
            skLineSegment(sketch, "E11.53.0.0", {"start": v(-8064.5, -3657.6) * mm, "end": v(-8064.5, -3619.5) * mm});
            skLineSegment(sketch, "E11.53.0.1", {"start": v(-8026.4, -3657.6) * mm, "end": v(-8026.4, -3619.5) * mm});
            skLineSegment(sketch, "E11.53.0.2", {"start": v(-8026.4, -3619.5) * mm, "end": v(-8064.5, -3619.5) * mm});
            skLineSegment(sketch, "E11.53.0.3", {"start": v(-8026.4, -3657.6) * mm, "end": v(-8064.5, -3657.6) * mm});
            skLineSegment(sketch, "E11.54.0.0", {"start": v(-8216.9, -3657.6) * mm, "end": v(-8216.9, -3619.5) * mm});
            skLineSegment(sketch, "E11.54.0.1", {"start": v(-8178.8, -3657.6) * mm, "end": v(-8178.8, -3619.5) * mm});
            skLineSegment(sketch, "E11.54.0.2", {"start": v(-8178.8, -3619.5) * mm, "end": v(-8216.9, -3619.5) * mm});
            skLineSegment(sketch, "E11.54.0.3", {"start": v(-8178.8, -3657.6) * mm, "end": v(-8216.9, -3657.6) * mm});
            skLineSegment(sketch, "E11.55.0.0", {"start": v(-8369.3, -3657.6) * mm, "end": v(-8369.3, -3619.5) * mm});
            skLineSegment(sketch, "E11.55.0.1", {"start": v(-8331.2, -3657.6) * mm, "end": v(-8331.2, -3619.5) * mm});
            skLineSegment(sketch, "E11.55.0.2", {"start": v(-8331.2, -3619.5) * mm, "end": v(-8369.3, -3619.5) * mm});
            skLineSegment(sketch, "E11.55.0.3", {"start": v(-8331.2, -3657.6) * mm, "end": v(-8369.3, -3657.6) * mm});
            skLineSegment(sketch, "E11.56.0.0", {"start": v(-8521.7, -3657.6) * mm, "end": v(-8521.7, -3619.5) * mm});
            skLineSegment(sketch, "E11.56.0.1", {"start": v(-8483.6, -3657.6) * mm, "end": v(-8483.6, -3619.5) * mm});
            skLineSegment(sketch, "E11.56.0.2", {"start": v(-8483.6, -3619.5) * mm, "end": v(-8521.7, -3619.5) * mm});
            skLineSegment(sketch, "E11.56.0.3", {"start": v(-8483.6, -3657.6) * mm, "end": v(-8521.7, -3657.6) * mm});
            skLineSegment(sketch, "E11.57.0.0", {"start": v(-8674.1, -3657.6) * mm, "end": v(-8674.1, -3619.5) * mm});
            skLineSegment(sketch, "E11.57.0.1", {"start": v(-8636, -3657.6) * mm, "end": v(-8636, -3619.5) * mm});
            skLineSegment(sketch, "E11.57.0.2", {"start": v(-8636, -3619.5) * mm, "end": v(-8674.1, -3619.5) * mm});
            skLineSegment(sketch, "E11.57.0.3", {"start": v(-8636, -3657.6) * mm, "end": v(-8674.1, -3657.6) * mm});
            skLineSegment(sketch, "E11.58.0.0", {"start": v(-8826.5, -3657.6) * mm, "end": v(-8826.5, -3619.5) * mm});
            skLineSegment(sketch, "E11.58.0.1", {"start": v(-8788.4, -3657.6) * mm, "end": v(-8788.4, -3619.5) * mm});
            skLineSegment(sketch, "E11.58.0.2", {"start": v(-8788.4, -3619.5) * mm, "end": v(-8826.5, -3619.5) * mm});
            skLineSegment(sketch, "E11.58.0.3", {"start": v(-8788.4, -3657.6) * mm, "end": v(-8826.5, -3657.6) * mm});
            skLineSegment(sketch, "E11.59.0.0", {"start": v(-8978.9, -3657.6) * mm, "end": v(-8978.9, -3619.5) * mm});
            skLineSegment(sketch, "E11.59.0.1", {"start": v(-8940.8, -3657.6) * mm, "end": v(-8940.8, -3619.5) * mm});
            skLineSegment(sketch, "E11.59.0.2", {"start": v(-8940.8, -3619.5) * mm, "end": v(-8978.9, -3619.5) * mm});
            skLineSegment(sketch, "E11.59.0.3", {"start": v(-8940.8, -3657.6) * mm, "end": v(-8978.9, -3657.6) * mm});
            skLineSegment(sketch, "E11.60.0.0", {"start": v(-9131.3, -3657.6) * mm, "end": v(-9131.3, -3619.5) * mm});
            skLineSegment(sketch, "E11.60.0.1", {"start": v(-9093.2, -3657.6) * mm, "end": v(-9093.2, -3619.5) * mm});
            skLineSegment(sketch, "E11.60.0.2", {"start": v(-9093.2, -3619.5) * mm, "end": v(-9131.3, -3619.5) * mm});
            skLineSegment(sketch, "E11.60.0.3", {"start": v(-9093.2, -3657.6) * mm, "end": v(-9131.3, -3657.6) * mm});
            skLineSegment(sketch, "E11.61.0.0", {"start": v(-9283.7, -3657.6) * mm, "end": v(-9283.7, -3619.5) * mm});
            skLineSegment(sketch, "E11.61.0.1", {"start": v(-9245.6, -3657.6) * mm, "end": v(-9245.6, -3619.5) * mm});
            skLineSegment(sketch, "E11.61.0.2", {"start": v(-9245.6, -3619.5) * mm, "end": v(-9283.7, -3619.5) * mm});
            skLineSegment(sketch, "E11.61.0.3", {"start": v(-9245.6, -3657.6) * mm, "end": v(-9283.7, -3657.6) * mm});
            skLineSegment(sketch, "E11.62.0.0", {"start": v(-9436.1, -3657.6) * mm, "end": v(-9436.1, -3619.5) * mm});
            skLineSegment(sketch, "E11.62.0.1", {"start": v(-9398, -3657.6) * mm, "end": v(-9398, -3619.5) * mm});
            skLineSegment(sketch, "E11.62.0.2", {"start": v(-9398, -3619.5) * mm, "end": v(-9436.1, -3619.5) * mm});
            skLineSegment(sketch, "E11.62.0.3", {"start": v(-9398, -3657.6) * mm, "end": v(-9436.1, -3657.6) * mm});
            skLineSegment(sketch, "E11.63.0.0", {"start": v(-9588.5, -3657.6) * mm, "end": v(-9588.5, -3619.5) * mm});
            skLineSegment(sketch, "E11.63.0.1", {"start": v(-9550.4, -3657.6) * mm, "end": v(-9550.4, -3619.5) * mm});
            skLineSegment(sketch, "E11.63.0.2", {"start": v(-9550.4, -3619.5) * mm, "end": v(-9588.5, -3619.5) * mm});
            skLineSegment(sketch, "E11.63.0.3", {"start": v(-9550.4, -3657.6) * mm, "end": v(-9588.5, -3657.6) * mm});
            skLineSegment(sketch, "E11.64.0.0", {"start": v(-9740.9, -3657.6) * mm, "end": v(-9740.9, -3619.5) * mm});
            skLineSegment(sketch, "E11.64.0.1", {"start": v(-9702.8, -3657.6) * mm, "end": v(-9702.8, -3619.5) * mm});
            skLineSegment(sketch, "E11.64.0.2", {"start": v(-9702.8, -3619.5) * mm, "end": v(-9740.9, -3619.5) * mm});
            skLineSegment(sketch, "E11.64.0.3", {"start": v(-9702.8, -3657.6) * mm, "end": v(-9740.9, -3657.6) * mm});
            skLineSegment(sketch, "E11.65.0.0", {"start": v(-9893.3, -3657.6) * mm, "end": v(-9893.3, -3619.5) * mm});
            skLineSegment(sketch, "E11.65.0.1", {"start": v(-9855.2, -3657.6) * mm, "end": v(-9855.2, -3619.5) * mm});
            skLineSegment(sketch, "E11.65.0.2", {"start": v(-9855.2, -3619.5) * mm, "end": v(-9893.3, -3619.5) * mm});
            skLineSegment(sketch, "E11.65.0.3", {"start": v(-9855.2, -3657.6) * mm, "end": v(-9893.3, -3657.6) * mm});
            skLineSegment(sketch, "E11.66.0.0", {"start": v(-10045.7, -3657.6) * mm, "end": v(-10045.7, -3619.5) * mm});
            skLineSegment(sketch, "E11.66.0.1", {"start": v(-10007.6, -3657.6) * mm, "end": v(-10007.6, -3619.5) * mm});
            skLineSegment(sketch, "E11.66.0.2", {"start": v(-10007.6, -3619.5) * mm, "end": v(-10045.7, -3619.5) * mm});
            skLineSegment(sketch, "E11.66.0.3", {"start": v(-10007.6, -3657.6) * mm, "end": v(-10045.7, -3657.6) * mm});
            skLineSegment(sketch, "E11.67.0.0", {"start": v(-10198.1, -3657.6) * mm, "end": v(-10198.1, -3619.5) * mm});
            skLineSegment(sketch, "E11.67.0.1", {"start": v(-10160, -3657.6) * mm, "end": v(-10160, -3619.5) * mm});
            skLineSegment(sketch, "E11.67.0.2", {"start": v(-10160, -3619.5) * mm, "end": v(-10198.1, -3619.5) * mm});
            skLineSegment(sketch, "E11.67.0.3", {"start": v(-10160, -3657.6) * mm, "end": v(-10198.1, -3657.6) * mm});
            skLineSegment(sketch, "E11.direction1", {"start": v(12.7, -3657.6) * mm, "end": v(-139.7, -3657.6) * mm, "construction": true});
            skLineSegment(sketch, "E12.0.68.0", {"start": v(-10350.5, -3657.6) * mm, "end": v(-10350.5, -3619.5) * mm});
            skLineSegment(sketch, "E12.3.68.0", {"start": v(-10312.4, -3657.6) * mm, "end": v(-10312.4, -3619.5) * mm});
            skLineSegment(sketch, "E12.6.68.0", {"start": v(-10312.4, -3619.5) * mm, "end": v(-10350.5, -3619.5) * mm});
            skLineSegment(sketch, "E12.9.68.0", {"start": v(-10312.4, -3657.6) * mm, "end": v(-10350.5, -3657.6) * mm});
            skLineSegment(sketch, "E12.0.69.0", {"start": v(-10502.9, -3657.6) * mm, "end": v(-10502.9, -3619.5) * mm});
            skLineSegment(sketch, "E12.3.69.0", {"start": v(-10464.8, -3657.6) * mm, "end": v(-10464.8, -3619.5) * mm});
            skLineSegment(sketch, "E12.6.69.0", {"start": v(-10464.8, -3619.5) * mm, "end": v(-10502.9, -3619.5) * mm});
            skLineSegment(sketch, "E12.9.69.0", {"start": v(-10464.8, -3657.6) * mm, "end": v(-10502.9, -3657.6) * mm});
            skLineSegment(sketch, "E12.0.70.0", {"start": v(-10655.3, -3657.6) * mm, "end": v(-10655.3, -3619.5) * mm});
            skLineSegment(sketch, "E12.3.70.0", {"start": v(-10617.2, -3657.6) * mm, "end": v(-10617.2, -3619.5) * mm});
            skLineSegment(sketch, "E12.6.70.0", {"start": v(-10617.2, -3619.5) * mm, "end": v(-10655.3, -3619.5) * mm});
            skLineSegment(sketch, "E12.9.70.0", {"start": v(-10617.2, -3657.6) * mm, "end": v(-10655.3, -3657.6) * mm});
            skLineSegment(sketch, "E12.0.71.0", {"start": v(-10807.7, -3657.6) * mm, "end": v(-10807.7, -3619.5) * mm});
            skLineSegment(sketch, "E12.3.71.0", {"start": v(-10769.6, -3657.6) * mm, "end": v(-10769.6, -3619.5) * mm});
            skLineSegment(sketch, "E12.6.71.0", {"start": v(-10769.6, -3619.5) * mm, "end": v(-10807.7, -3619.5) * mm});
            skLineSegment(sketch, "E12.9.71.0", {"start": v(-10769.6, -3657.6) * mm, "end": v(-10807.7, -3657.6) * mm});
            skLineSegment(sketch, "E12.0.72.0", {"start": v(-10960.1, -3657.6) * mm, "end": v(-10960.1, -3619.5) * mm});
            skLineSegment(sketch, "E12.3.72.0", {"start": v(-10922, -3657.6) * mm, "end": v(-10922, -3619.5) * mm});
            skLineSegment(sketch, "E12.6.72.0", {"start": v(-10922, -3619.5) * mm, "end": v(-10960.1, -3619.5) * mm});
            skLineSegment(sketch, "E12.9.72.0", {"start": v(-10922, -3657.6) * mm, "end": v(-10960.1, -3657.6) * mm});
            skLineSegment(sketch, "E12.0.73.0", {"start": v(-11112.5, -3657.6) * mm, "end": v(-11112.5, -3619.5) * mm});
            skLineSegment(sketch, "E12.3.73.0", {"start": v(-11074.4, -3657.6) * mm, "end": v(-11074.4, -3619.5) * mm});
            skLineSegment(sketch, "E12.6.73.0", {"start": v(-11074.4, -3619.5) * mm, "end": v(-11112.5, -3619.5) * mm});
            skLineSegment(sketch, "E12.9.73.0", {"start": v(-11074.4, -3657.6) * mm, "end": v(-11112.5, -3657.6) * mm});
            skLineSegment(sketch, "E12.0.74.0", {"start": v(-11264.9, -3657.6) * mm, "end": v(-11264.9, -3619.5) * mm});
            skLineSegment(sketch, "E12.3.74.0", {"start": v(-11226.8, -3657.6) * mm, "end": v(-11226.8, -3619.5) * mm});
            skLineSegment(sketch, "E12.6.74.0", {"start": v(-11226.8, -3619.5) * mm, "end": v(-11264.9, -3619.5) * mm});
            skLineSegment(sketch, "E12.9.74.0", {"start": v(-11226.8, -3657.6) * mm, "end": v(-11264.9, -3657.6) * mm});
            skLineSegment(sketch, "E12.0.75.0", {"start": v(-11417.3, -3657.6) * mm, "end": v(-11417.3, -3619.5) * mm});
            skLineSegment(sketch, "E12.3.75.0", {"start": v(-11379.2, -3657.6) * mm, "end": v(-11379.2, -3619.5) * mm});
            skLineSegment(sketch, "E12.6.75.0", {"start": v(-11379.2, -3619.5) * mm, "end": v(-11417.3, -3619.5) * mm});
            skLineSegment(sketch, "E12.9.75.0", {"start": v(-11379.2, -3657.6) * mm, "end": v(-11417.3, -3657.6) * mm});
            skLineSegment(sketch, "E13.bottom", {"start": v(-11531.6, -3657.6) * mm, "end": v(-11493.5, -3657.6) * mm});
            skLineSegment(sketch, "E13.top", {"start": v(-11531.6, -3619.5) * mm, "end": v(-11493.5, -3619.5) * mm});
            skLineSegment(sketch, "E13.left", {"start": v(-11531.6, -3657.6) * mm, "end": v(-11531.6, -3619.5) * mm});
            skLineSegment(sketch, "E13.right", {"start": v(-11493.5, -3657.6) * mm, "end": v(-11493.5, -3619.5) * mm});
            skLineSegment(sketch, "E14.bottom", {"start": v(-11531.6, 0) * mm, "end": v(-11493.5, 0) * mm});
            skLineSegment(sketch, "E14.top", {"start": v(-11531.6, -38.1) * mm, "end": v(-11493.5, -38.1) * mm});
            skLineSegment(sketch, "E14.left", {"start": v(-11531.6, 0) * mm, "end": v(-11531.6, -38.1) * mm});
            skLineSegment(sketch, "E14.right", {"start": v(-11493.5, 0) * mm, "end": v(-11493.5, -38.1) * mm});
            skLineSegment(sketch, "E15.0.1.0", {"start": v(-11531.6, -152.4) * mm, "end": v(-11493.5, -152.4) * mm});
            skLineSegment(sketch, "E15.0.1.1", {"start": v(-11531.6, -190.5) * mm, "end": v(-11493.5, -190.5) * mm});
            skLineSegment(sketch, "E15.0.1.2", {"start": v(-11531.6, -152.4) * mm, "end": v(-11531.6, -190.5) * mm});
            skLineSegment(sketch, "E15.0.1.3", {"start": v(-11493.5, -152.4) * mm, "end": v(-11493.5, -190.5) * mm});
            skLineSegment(sketch, "E15.0.2.0", {"start": v(-11531.6, -304.8) * mm, "end": v(-11493.5, -304.8) * mm});
            skLineSegment(sketch, "E15.0.2.1", {"start": v(-11531.6, -342.9) * mm, "end": v(-11493.5, -342.9) * mm});
            skLineSegment(sketch, "E15.0.2.2", {"start": v(-11531.6, -304.8) * mm, "end": v(-11531.6, -342.9) * mm});
            skLineSegment(sketch, "E15.0.2.3", {"start": v(-11493.5, -304.8) * mm, "end": v(-11493.5, -342.9) * mm});
            skLineSegment(sketch, "E15.0.3.0", {"start": v(-11531.6, -457.2) * mm, "end": v(-11493.5, -457.2) * mm});
            skLineSegment(sketch, "E15.0.3.1", {"start": v(-11531.6, -495.3) * mm, "end": v(-11493.5, -495.3) * mm});
            skLineSegment(sketch, "E15.0.3.2", {"start": v(-11531.6, -457.2) * mm, "end": v(-11531.6, -495.3) * mm});
            skLineSegment(sketch, "E15.0.3.3", {"start": v(-11493.5, -457.2) * mm, "end": v(-11493.5, -495.3) * mm});
            skLineSegment(sketch, "E15.0.4.0", {"start": v(-11531.6, -609.6) * mm, "end": v(-11493.5, -609.6) * mm});
            skLineSegment(sketch, "E15.0.4.1", {"start": v(-11531.6, -647.7) * mm, "end": v(-11493.5, -647.7) * mm});
            skLineSegment(sketch, "E15.0.4.2", {"start": v(-11531.6, -609.6) * mm, "end": v(-11531.6, -647.7) * mm});
            skLineSegment(sketch, "E15.0.4.3", {"start": v(-11493.5, -609.6) * mm, "end": v(-11493.5, -647.7) * mm});
            skLineSegment(sketch, "E15.0.5.0", {"start": v(-11531.6, -762) * mm, "end": v(-11493.5, -762) * mm});
            skLineSegment(sketch, "E15.0.5.1", {"start": v(-11531.6, -800.1) * mm, "end": v(-11493.5, -800.1) * mm});
            skLineSegment(sketch, "E15.0.5.2", {"start": v(-11531.6, -762) * mm, "end": v(-11531.6, -800.1) * mm});
            skLineSegment(sketch, "E15.0.5.3", {"start": v(-11493.5, -762) * mm, "end": v(-11493.5, -800.1) * mm});
            skLineSegment(sketch, "E15.0.6.0", {"start": v(-11531.6, -914.4) * mm, "end": v(-11493.5, -914.4) * mm});
            skLineSegment(sketch, "E15.0.6.1", {"start": v(-11531.6, -952.5) * mm, "end": v(-11493.5, -952.5) * mm});
            skLineSegment(sketch, "E15.0.6.2", {"start": v(-11531.6, -914.4) * mm, "end": v(-11531.6, -952.5) * mm});
            skLineSegment(sketch, "E15.0.6.3", {"start": v(-11493.5, -914.4) * mm, "end": v(-11493.5, -952.5) * mm});
            skLineSegment(sketch, "E15.0.7.0", {"start": v(-11531.6, -1066.8) * mm, "end": v(-11493.5, -1066.8) * mm});
            skLineSegment(sketch, "E15.0.7.1", {"start": v(-11531.6, -1104.9) * mm, "end": v(-11493.5, -1104.9) * mm});
            skLineSegment(sketch, "E15.0.7.2", {"start": v(-11531.6, -1066.8) * mm, "end": v(-11531.6, -1104.9) * mm});
            skLineSegment(sketch, "E15.0.7.3", {"start": v(-11493.5, -1066.8) * mm, "end": v(-11493.5, -1104.9) * mm});
            skLineSegment(sketch, "E15.0.8.0", {"start": v(-11531.6, -1219.2) * mm, "end": v(-11493.5, -1219.2) * mm});
            skLineSegment(sketch, "E15.0.8.1", {"start": v(-11531.6, -1257.3) * mm, "end": v(-11493.5, -1257.3) * mm});
            skLineSegment(sketch, "E15.0.8.2", {"start": v(-11531.6, -1219.2) * mm, "end": v(-11531.6, -1257.3) * mm});
            skLineSegment(sketch, "E15.0.8.3", {"start": v(-11493.5, -1219.2) * mm, "end": v(-11493.5, -1257.3) * mm});
            skLineSegment(sketch, "E15.0.9.0", {"start": v(-11531.6, -1371.6) * mm, "end": v(-11493.5, -1371.6) * mm});
            skLineSegment(sketch, "E15.0.9.1", {"start": v(-11531.6, -1409.7) * mm, "end": v(-11493.5, -1409.7) * mm});
            skLineSegment(sketch, "E15.0.9.2", {"start": v(-11531.6, -1371.6) * mm, "end": v(-11531.6, -1409.7) * mm});
            skLineSegment(sketch, "E15.0.9.3", {"start": v(-11493.5, -1371.6) * mm, "end": v(-11493.5, -1409.7) * mm});
            skLineSegment(sketch, "E15.0.10.0", {"start": v(-11531.6, -1524) * mm, "end": v(-11493.5, -1524) * mm});
            skLineSegment(sketch, "E15.0.10.1", {"start": v(-11531.6, -1562.1) * mm, "end": v(-11493.5, -1562.1) * mm});
            skLineSegment(sketch, "E15.0.10.2", {"start": v(-11531.6, -1524) * mm, "end": v(-11531.6, -1562.1) * mm});
            skLineSegment(sketch, "E15.0.10.3", {"start": v(-11493.5, -1524) * mm, "end": v(-11493.5, -1562.1) * mm});
            skLineSegment(sketch, "E15.0.11.0", {"start": v(-11531.6, -1676.4) * mm, "end": v(-11493.5, -1676.4) * mm});
            skLineSegment(sketch, "E15.0.11.1", {"start": v(-11531.6, -1714.5) * mm, "end": v(-11493.5, -1714.5) * mm});
            skLineSegment(sketch, "E15.0.11.2", {"start": v(-11531.6, -1676.4) * mm, "end": v(-11531.6, -1714.5) * mm});
            skLineSegment(sketch, "E15.0.11.3", {"start": v(-11493.5, -1676.4) * mm, "end": v(-11493.5, -1714.5) * mm});
            skLineSegment(sketch, "E15.0.12.0", {"start": v(-11531.6, -1828.8) * mm, "end": v(-11493.5, -1828.8) * mm});
            skLineSegment(sketch, "E15.0.12.1", {"start": v(-11531.6, -1866.9) * mm, "end": v(-11493.5, -1866.9) * mm});
            skLineSegment(sketch, "E15.0.12.2", {"start": v(-11531.6, -1828.8) * mm, "end": v(-11531.6, -1866.9) * mm});
            skLineSegment(sketch, "E15.0.12.3", {"start": v(-11493.5, -1828.8) * mm, "end": v(-11493.5, -1866.9) * mm});
            skLineSegment(sketch, "E15.0.13.0", {"start": v(-11531.6, -1981.2) * mm, "end": v(-11493.5, -1981.2) * mm});
            skLineSegment(sketch, "E15.0.13.1", {"start": v(-11531.6, -2019.3) * mm, "end": v(-11493.5, -2019.3) * mm});
            skLineSegment(sketch, "E15.0.13.2", {"start": v(-11531.6, -1981.2) * mm, "end": v(-11531.6, -2019.3) * mm});
            skLineSegment(sketch, "E15.0.13.3", {"start": v(-11493.5, -1981.2) * mm, "end": v(-11493.5, -2019.3) * mm});
            skLineSegment(sketch, "E15.0.14.0", {"start": v(-11531.6, -2133.6) * mm, "end": v(-11493.5, -2133.6) * mm});
            skLineSegment(sketch, "E15.0.14.1", {"start": v(-11531.6, -2171.7) * mm, "end": v(-11493.5, -2171.7) * mm});
            skLineSegment(sketch, "E15.0.14.2", {"start": v(-11531.6, -2133.6) * mm, "end": v(-11531.6, -2171.7) * mm});
            skLineSegment(sketch, "E15.0.14.3", {"start": v(-11493.5, -2133.6) * mm, "end": v(-11493.5, -2171.7) * mm});
            skLineSegment(sketch, "E15.0.15.0", {"start": v(-11531.6, -2286) * mm, "end": v(-11493.5, -2286) * mm});
            skLineSegment(sketch, "E15.0.15.1", {"start": v(-11531.6, -2324.1) * mm, "end": v(-11493.5, -2324.1) * mm});
            skLineSegment(sketch, "E15.0.15.2", {"start": v(-11531.6, -2286) * mm, "end": v(-11531.6, -2324.1) * mm});
            skLineSegment(sketch, "E15.0.15.3", {"start": v(-11493.5, -2286) * mm, "end": v(-11493.5, -2324.1) * mm});
            skLineSegment(sketch, "E15.0.16.0", {"start": v(-11531.6, -2438.4) * mm, "end": v(-11493.5, -2438.4) * mm});
            skLineSegment(sketch, "E15.0.16.1", {"start": v(-11531.6, -2476.5) * mm, "end": v(-11493.5, -2476.5) * mm});
            skLineSegment(sketch, "E15.0.16.2", {"start": v(-11531.6, -2438.4) * mm, "end": v(-11531.6, -2476.5) * mm});
            skLineSegment(sketch, "E15.0.16.3", {"start": v(-11493.5, -2438.4) * mm, "end": v(-11493.5, -2476.5) * mm});
            skLineSegment(sketch, "E15.0.17.0", {"start": v(-11531.6, -2590.8) * mm, "end": v(-11493.5, -2590.8) * mm});
            skLineSegment(sketch, "E15.0.17.1", {"start": v(-11531.6, -2628.9) * mm, "end": v(-11493.5, -2628.9) * mm});
            skLineSegment(sketch, "E15.0.17.2", {"start": v(-11531.6, -2590.8) * mm, "end": v(-11531.6, -2628.9) * mm});
            skLineSegment(sketch, "E15.0.17.3", {"start": v(-11493.5, -2590.8) * mm, "end": v(-11493.5, -2628.9) * mm});
            skLineSegment(sketch, "E15.0.18.0", {"start": v(-11531.6, -2743.2) * mm, "end": v(-11493.5, -2743.2) * mm});
            skLineSegment(sketch, "E15.0.18.1", {"start": v(-11531.6, -2781.3) * mm, "end": v(-11493.5, -2781.3) * mm});
            skLineSegment(sketch, "E15.0.18.2", {"start": v(-11531.6, -2743.2) * mm, "end": v(-11531.6, -2781.3) * mm});
            skLineSegment(sketch, "E15.0.18.3", {"start": v(-11493.5, -2743.2) * mm, "end": v(-11493.5, -2781.3) * mm});
            skLineSegment(sketch, "E15.0.19.0", {"start": v(-11531.6, -2895.6) * mm, "end": v(-11493.5, -2895.6) * mm});
            skLineSegment(sketch, "E15.0.19.1", {"start": v(-11531.6, -2933.7) * mm, "end": v(-11493.5, -2933.7) * mm});
            skLineSegment(sketch, "E15.0.19.2", {"start": v(-11531.6, -2895.6) * mm, "end": v(-11531.6, -2933.7) * mm});
            skLineSegment(sketch, "E15.0.19.3", {"start": v(-11493.5, -2895.6) * mm, "end": v(-11493.5, -2933.7) * mm});
            skLineSegment(sketch, "E15.0.20.0", {"start": v(-11531.6, -3048) * mm, "end": v(-11493.5, -3048) * mm});
            skLineSegment(sketch, "E15.0.20.1", {"start": v(-11531.6, -3086.1) * mm, "end": v(-11493.5, -3086.1) * mm});
            skLineSegment(sketch, "E15.0.20.2", {"start": v(-11531.6, -3048) * mm, "end": v(-11531.6, -3086.1) * mm});
            skLineSegment(sketch, "E15.0.20.3", {"start": v(-11493.5, -3048) * mm, "end": v(-11493.5, -3086.1) * mm});
            skLineSegment(sketch, "E15.0.21.0", {"start": v(-11531.6, -3200.4) * mm, "end": v(-11493.5, -3200.4) * mm});
            skLineSegment(sketch, "E15.0.21.1", {"start": v(-11531.6, -3238.5) * mm, "end": v(-11493.5, -3238.5) * mm});
            skLineSegment(sketch, "E15.0.21.2", {"start": v(-11531.6, -3200.4) * mm, "end": v(-11531.6, -3238.5) * mm});
            skLineSegment(sketch, "E15.0.21.3", {"start": v(-11493.5, -3200.4) * mm, "end": v(-11493.5, -3238.5) * mm});
            skLineSegment(sketch, "E15.0.22.0", {"start": v(-11531.6, -3352.8) * mm, "end": v(-11493.5, -3352.8) * mm});
            skLineSegment(sketch, "E15.0.22.1", {"start": v(-11531.6, -3390.9) * mm, "end": v(-11493.5, -3390.9) * mm});
            skLineSegment(sketch, "E15.0.22.2", {"start": v(-11531.6, -3352.8) * mm, "end": v(-11531.6, -3390.9) * mm});
            skLineSegment(sketch, "E15.0.22.3", {"start": v(-11493.5, -3352.8) * mm, "end": v(-11493.5, -3390.9) * mm});
            skLineSegment(sketch, "E15.0.23.0", {"start": v(-11531.6, -3505.2) * mm, "end": v(-11493.5, -3505.2) * mm});
            skLineSegment(sketch, "E15.0.23.1", {"start": v(-11531.6, -3543.3) * mm, "end": v(-11493.5, -3543.3) * mm});
            skLineSegment(sketch, "E15.0.23.2", {"start": v(-11531.6, -3505.2) * mm, "end": v(-11531.6, -3543.3) * mm});
            skLineSegment(sketch, "E15.0.23.3", {"start": v(-11493.5, -3505.2) * mm, "end": v(-11493.5, -3543.3) * mm});
            skLineSegment(sketch, "E15.direction1", {"start": v(-11531.6, 0) * mm, "end": v(-11506.2, 0) * mm, "construction": true});
            skLineSegment(sketch, "E15.direction2", {"start": v(-11531.6, 0) * mm, "end": v(-11531.6, -152.4) * mm, "construction": true});
            skSolve(sketch);
        }
        {
            var Q0;
            Q0=makeQuery(id+"F0.imprint","IMPRINT",FACE,{"disambiguationData":[TD([[makeQuery(id+"F0.imprint","IMPRINT",EDGE,{"derivedFrom":sQuery(id+"F0.wireOp",EDGE,"E12.0.74.0")}),-1.0]])]});
            var Q1;
            Q1=makeQuery(id+"F0.imprint","IMPRINT",FACE,{"disambiguationData":[TD([[makeQuery(id+"F0.imprint","IMPRINT",EDGE,{"derivedFrom":sQuery(id+"F0.wireOp",EDGE,"E11.58.0.0")}),-1.0]])]});
            var Q2;
            Q2=makeQuery(id+"F0.imprint","IMPRINT",FACE,{"disambiguationData":[TD([[makeQuery(id+"F0.imprint","IMPRINT",EDGE,{"derivedFrom":sQuery(id+"F0.wireOp",EDGE,"E12.0.73.0")}),-1.0]])]});
            var Q3;
            Q3=makeQuery(id+"F0.imprint","IMPRINT",FACE,{"disambiguationData":[TD([[makeQuery(id+"F0.imprint","IMPRINT",EDGE,{"derivedFrom":sQuery(id+"F0.wireOp",EDGE,"E12.0.72.0")}),-1.0]])]});
            var Q4;
            Q4=makeQuery(id+"F0.imprint","IMPRINT",FACE,{"disambiguationData":[TD([[makeQuery(id+"F0.imprint","IMPRINT",EDGE,{"derivedFrom":sQuery(id+"F0.wireOp",EDGE,"E12.0.70.0")}),-1.0]])]});
            var Q5;
            Q5=makeQuery(id+"F0.imprint","IMPRINT",FACE,{"disambiguationData":[TD([[makeQuery(id+"F0.imprint","IMPRINT",EDGE,{"derivedFrom":sQuery(id+"F0.wireOp",EDGE,"E12.0.69.0")}),-1.0]])]});
            var Q6;
            Q6=makeQuery(id+"F0.imprint","IMPRINT",FACE,{"disambiguationData":[TD([[makeQuery(id+"F0.imprint","IMPRINT",EDGE,{"derivedFrom":sQuery(id+"F0.wireOp",EDGE,"E12.0.71.0")}),-1.0]])]});
            var Q7;
            Q7=makeQuery(id+"F0.imprint","IMPRINT",FACE,{"disambiguationData":[TD([[makeQuery(id+"F0.imprint","IMPRINT",EDGE,{"derivedFrom":sQuery(id+"F0.wireOp",EDGE,"E11.59.0.0")}),-1.0]])]});
            var Q8;
            Q8=makeQuery(id+"F0.imprint","IMPRINT",FACE,{"disambiguationData":[TD([[makeQuery(id+"F0.imprint","IMPRINT",EDGE,{"derivedFrom":sQuery(id+"F0.wireOp",EDGE,"E12.0.75.0")}),-1.0]])]});
            var Q9;
            Q9=makeQuery(id+"F0.imprint","IMPRINT",FACE,{"disambiguationData":[TD([[makeQuery(id+"F0.imprint","IMPRINT",EDGE,{"derivedFrom":sQuery(id+"F0.wireOp",EDGE,"E11.60.0.0")}),-1.0]])]});
            var Q10;
            Q10=makeQuery(id+"F0.imprint","IMPRINT",FACE,{"disambiguationData":[TD([[makeQuery(id+"F0.imprint","IMPRINT",EDGE,{"derivedFrom":sQuery(id+"F0.wireOp",EDGE,"E13.bottom")}),1.0]])]});
            var Q11;
            Q11=makeQuery(id+"F0.imprint","IMPRINT",FACE,{"disambiguationData":[TD([[makeQuery(id+"F0.imprint","IMPRINT",EDGE,{"derivedFrom":sQuery(id+"F0.wireOp",EDGE,"E11.61.0.0")}),-1.0]])]});
            var Q12;
            Q12=makeQuery(id+"F0.imprint","IMPRINT",FACE,{"disambiguationData":[TD([[makeQuery(id+"F0.imprint","IMPRINT",EDGE,{"derivedFrom":sQuery(id+"F0.wireOp",EDGE,"E15.0.17.0")}),-1.0]])]});
            var Q13;
            Q13=makeQuery(id+"F0.imprint","IMPRINT",FACE,{"disambiguationData":[TD([[makeQuery(id+"F0.imprint","IMPRINT",EDGE,{"derivedFrom":sQuery(id+"F0.wireOp",EDGE,"E11.62.0.0")}),-1.0]])]});
            var Q14;
            Q14=makeQuery(id+"F0.imprint","IMPRINT",FACE,{"disambiguationData":[TD([[makeQuery(id+"F0.imprint","IMPRINT",EDGE,{"derivedFrom":sQuery(id+"F0.wireOp",EDGE,"E15.0.18.0")}),-1.0]])]});
            var Q15;
            Q15=makeQuery(id+"F0.imprint","IMPRINT",FACE,{"disambiguationData":[TD([[makeQuery(id+"F0.imprint","IMPRINT",EDGE,{"derivedFrom":sQuery(id+"F0.wireOp",EDGE,"E11.63.0.0")}),-1.0]])]});
            var Q16;
            Q16=makeQuery(id+"F0.imprint","IMPRINT",FACE,{"disambiguationData":[TD([[makeQuery(id+"F0.imprint","IMPRINT",EDGE,{"derivedFrom":sQuery(id+"F0.wireOp",EDGE,"E15.0.19.0")}),-1.0]])]});
            var Q17;
            Q17=makeQuery(id+"F0.imprint","IMPRINT",FACE,{"disambiguationData":[TD([[makeQuery(id+"F0.imprint","IMPRINT",EDGE,{"derivedFrom":sQuery(id+"F0.wireOp",EDGE,"E11.64.0.0")}),-1.0]])]});
            var Q18;
            Q18=makeQuery(id+"F0.imprint","IMPRINT",FACE,{"disambiguationData":[TD([[makeQuery(id+"F0.imprint","IMPRINT",EDGE,{"derivedFrom":sQuery(id+"F0.wireOp",EDGE,"E15.0.20.0")}),-1.0]])]});
            var Q19;
            Q19=makeQuery(id+"F0.imprint","IMPRINT",FACE,{"disambiguationData":[TD([[makeQuery(id+"F0.imprint","IMPRINT",EDGE,{"derivedFrom":sQuery(id+"F0.wireOp",EDGE,"E11.65.0.0")}),-1.0]])]});
            var Q20;
            Q20=makeQuery(id+"F0.imprint","IMPRINT",FACE,{"disambiguationData":[TD([[makeQuery(id+"F0.imprint","IMPRINT",EDGE,{"derivedFrom":sQuery(id+"F0.wireOp",EDGE,"E15.0.21.0")}),-1.0]])]});
            var Q21;
            Q21=makeQuery(id+"F0.imprint","IMPRINT",FACE,{"disambiguationData":[TD([[makeQuery(id+"F0.imprint","IMPRINT",EDGE,{"derivedFrom":sQuery(id+"F0.wireOp",EDGE,"E11.66.0.0")}),-1.0]])]});
            var Q22;
            Q22=makeQuery(id+"F0.imprint","IMPRINT",FACE,{"disambiguationData":[TD([[makeQuery(id+"F0.imprint","IMPRINT",EDGE,{"derivedFrom":sQuery(id+"F0.wireOp",EDGE,"E15.0.22.0")}),-1.0]])]});
            var Q23;
            Q23=makeQuery(id+"F0.imprint","IMPRINT",FACE,{"disambiguationData":[TD([[makeQuery(id+"F0.imprint","IMPRINT",EDGE,{"derivedFrom":sQuery(id+"F0.wireOp",EDGE,"E11.67.0.0")}),-1.0]])]});
            var Q24;
            Q24=makeQuery(id+"F0.imprint","IMPRINT",FACE,{"disambiguationData":[TD([[makeQuery(id+"F0.imprint","IMPRINT",EDGE,{"derivedFrom":sQuery(id+"F0.wireOp",EDGE,"E15.0.23.0")}),-1.0]])]});
            var Q25;
            Q25=makeQuery(id+"F0.imprint","IMPRINT",FACE,{"disambiguationData":[TD([[makeQuery(id+"F0.imprint","IMPRINT",EDGE,{"derivedFrom":sQuery(id+"F0.wireOp",EDGE,"E12.0.68.0")}),-1.0]])]});
            var Q26;
            Q26=makeQuery(id+"F0.imprint","IMPRINT",FACE,{"disambiguationData":[TD([[makeQuery(id+"F0.imprint","IMPRINT",EDGE,{"derivedFrom":sQuery(id+"F0.wireOp",EDGE,"E15.0.12.0")}),-1.0]])]});
            var Q27;
            Q27=makeQuery(id+"F0.imprint","IMPRINT",FACE,{"disambiguationData":[TD([[makeQuery(id+"F0.imprint","IMPRINT",EDGE,{"derivedFrom":sQuery(id+"F0.wireOp",EDGE,"E15.0.14.0")}),-1.0]])]});
            var Q28;
            Q28=makeQuery(id+"F0.imprint","IMPRINT",FACE,{"disambiguationData":[TD([[makeQuery(id+"F0.imprint","IMPRINT",EDGE,{"derivedFrom":sQuery(id+"F0.wireOp",EDGE,"E15.0.1.0")}),-1.0]])]});
            var Q29;
            Q29=makeQuery(id+"F0.imprint","IMPRINT",FACE,{"disambiguationData":[TD([[makeQuery(id+"F0.imprint","IMPRINT",EDGE,{"derivedFrom":sQuery(id+"F0.wireOp",EDGE,"E15.0.6.0")}),-1.0]])]});
            var Q30;
            Q30=makeQuery(id+"F0.imprint","IMPRINT",FACE,{"disambiguationData":[TD([[makeQuery(id+"F0.imprint","IMPRINT",EDGE,{"derivedFrom":sQuery(id+"F0.wireOp",EDGE,"E15.0.13.0")}),-1.0]])]});
            var Q31;
            Q31=makeQuery(id+"F0.imprint","IMPRINT",FACE,{"disambiguationData":[TD([[makeQuery(id+"F0.imprint","IMPRINT",EDGE,{"derivedFrom":sQuery(id+"F0.wireOp",EDGE,"E15.0.11.0")}),-1.0]])]});
            var Q32;
            Q32=makeQuery(id+"F0.imprint","IMPRINT",FACE,{"disambiguationData":[TD([[makeQuery(id+"F0.imprint","IMPRINT",EDGE,{"derivedFrom":sQuery(id+"F0.wireOp",EDGE,"E15.0.9.0")}),-1.0]])]});
            var Q33;
            Q33=makeQuery(id+"F0.imprint","IMPRINT",FACE,{"disambiguationData":[TD([[makeQuery(id+"F0.imprint","IMPRINT",EDGE,{"derivedFrom":sQuery(id+"F0.wireOp",EDGE,"E15.0.8.0")}),-1.0]])]});
            var Q34;
            Q34=makeQuery(id+"F0.imprint","IMPRINT",FACE,{"disambiguationData":[TD([[makeQuery(id+"F0.imprint","IMPRINT",EDGE,{"derivedFrom":sQuery(id+"F0.wireOp",EDGE,"E15.0.10.0")}),-1.0]])]});
            var Q35;
            Q35=makeQuery(id+"F0.imprint","IMPRINT",FACE,{"disambiguationData":[TD([[makeQuery(id+"F0.imprint","IMPRINT",EDGE,{"derivedFrom":sQuery(id+"F0.wireOp",EDGE,"E15.0.15.0")}),-1.0]])]});
            var Q36;
            Q36=makeQuery(id+"F0.imprint","IMPRINT",FACE,{"disambiguationData":[TD([[makeQuery(id+"F0.imprint","IMPRINT",EDGE,{"derivedFrom":sQuery(id+"F0.wireOp",EDGE,"E15.0.16.0")}),-1.0]])]});
            var Q37;
            Q37=makeQuery(id+"F0.imprint","IMPRINT",FACE,{"disambiguationData":[TD([[makeQuery(id+"F0.imprint","IMPRINT",EDGE,{"derivedFrom":sQuery(id+"F0.wireOp",EDGE,"E15.0.2.0")}),-1.0]])]});
            var Q38;
            Q38=makeQuery(id+"F0.imprint","IMPRINT",FACE,{"disambiguationData":[TD([[makeQuery(id+"F0.imprint","IMPRINT",EDGE,{"derivedFrom":sQuery(id+"F0.wireOp",EDGE,"E15.0.3.0")}),-1.0]])]});
            var Q39;
            Q39=makeQuery(id+"F0.imprint","IMPRINT",FACE,{"disambiguationData":[TD([[makeQuery(id+"F0.imprint","IMPRINT",EDGE,{"derivedFrom":sQuery(id+"F0.wireOp",EDGE,"E15.0.4.0")}),-1.0]])]});
            var Q40;
            Q40=makeQuery(id+"F0.imprint","IMPRINT",FACE,{"disambiguationData":[TD([[makeQuery(id+"F0.imprint","IMPRINT",EDGE,{"derivedFrom":sQuery(id+"F0.wireOp",EDGE,"E15.0.5.0")}),-1.0]])]});
            var Q41;
            Q41=makeQuery(id+"F0.imprint","IMPRINT",FACE,{"disambiguationData":[TD([[makeQuery(id+"F0.imprint","IMPRINT",EDGE,{"derivedFrom":sQuery(id+"F0.wireOp",EDGE,"E15.0.7.0")}),-1.0]])]});
            var Q42;
            Q42=makeQuery(id+"F0.imprint","IMPRINT",FACE,{"disambiguationData":[TD([[makeQuery(id+"F0.imprint","IMPRINT",EDGE,{"derivedFrom":sQuery(id+"F0.wireOp",EDGE,"E14.bottom")}),-1.0]])]});
            var Q43;
            Q43=makeQuery(id+"F0.imprint","IMPRINT",FACE,{"disambiguationData":[TD([[makeQuery(id+"F0.imprint","IMPRINT",EDGE,{"derivedFrom":sQuery(id+"F0.wireOp",EDGE,"E11.24.0.0")}),-1.0]])]});
            var Q44;
            Q44=makeQuery(id+"F0.imprint","IMPRINT",FACE,{"disambiguationData":[TD([[makeQuery(id+"F0.imprint","IMPRINT",EDGE,{"derivedFrom":sQuery(id+"F0.wireOp",EDGE,"E11.56.0.0")}),-1.0]])]});
            var Q45;
            Q45=makeQuery(id+"F0.imprint","IMPRINT",FACE,{"disambiguationData":[TD([[makeQuery(id+"F0.imprint","IMPRINT",EDGE,{"derivedFrom":sQuery(id+"F0.wireOp",EDGE,"E11.10.0.0")}),-1.0]])]});
            var Q46;
            Q46=makeQuery(id+"F0.imprint","IMPRINT",FACE,{"disambiguationData":[TD([[makeQuery(id+"F0.imprint","IMPRINT",EDGE,{"derivedFrom":sQuery(id+"F0.wireOp",EDGE,"E11.26.0.0")}),-1.0]])]});
            var Q47;
            Q47=makeQuery(id+"F0.imprint","IMPRINT",FACE,{"disambiguationData":[TD([[makeQuery(id+"F0.imprint","IMPRINT",EDGE,{"derivedFrom":sQuery(id+"F0.wireOp",EDGE,"E11.42.0.0")}),-1.0]])]});
            var Q48;
            Q48=makeQuery(id+"F0.imprint","IMPRINT",FACE,{"disambiguationData":[TD([[makeQuery(id+"F0.imprint","IMPRINT",EDGE,{"derivedFrom":sQuery(id+"F0.wireOp",EDGE,"E11.25.0.0")}),-1.0]])]});
            var Q49;
            Q49=makeQuery(id+"F0.imprint","IMPRINT",FACE,{"disambiguationData":[TD([[makeQuery(id+"F0.imprint","IMPRINT",EDGE,{"derivedFrom":sQuery(id+"F0.wireOp",EDGE,"E11.6.0.0")}),-1.0]])]});
            var Q50;
            Q50=makeQuery(id+"F0.imprint","IMPRINT",FACE,{"disambiguationData":[TD([[makeQuery(id+"F0.imprint","IMPRINT",EDGE,{"derivedFrom":sQuery(id+"F0.wireOp",EDGE,"E11.38.0.0")}),-1.0]])]});
            var Q51;
            Q51=makeQuery(id+"F0.imprint","IMPRINT",FACE,{"disambiguationData":[TD([[makeQuery(id+"F0.imprint","IMPRINT",EDGE,{"derivedFrom":sQuery(id+"F0.wireOp",EDGE,"E11.21.0.0")}),-1.0]])]});
            var Q52;
            Q52=makeQuery(id+"F0.imprint","IMPRINT",FACE,{"disambiguationData":[TD([[makeQuery(id+"F0.imprint","IMPRINT",EDGE,{"derivedFrom":sQuery(id+"F0.wireOp",EDGE,"E11.53.0.0")}),-1.0]])]});
            var Q53;
            Q53=makeQuery(id+"F0.imprint","IMPRINT",FACE,{"disambiguationData":[TD([[makeQuery(id+"F0.imprint","IMPRINT",EDGE,{"derivedFrom":sQuery(id+"F0.wireOp",EDGE,"E11.39.0.0")}),-1.0]])]});
            var Q54;
            Q54=makeQuery(id+"F0.imprint","IMPRINT",FACE,{"disambiguationData":[TD([[makeQuery(id+"F0.imprint","IMPRINT",EDGE,{"derivedFrom":sQuery(id+"F0.wireOp",EDGE,"E11.7.0.0")}),-1.0]])]});
            var Q55;
            Q55=makeQuery(id+"F0.imprint","IMPRINT",FACE,{"disambiguationData":[TD([[makeQuery(id+"F0.imprint","IMPRINT",EDGE,{"derivedFrom":sQuery(id+"F0.wireOp",EDGE,"E11.43.0.0")}),-1.0]])]});
            var Q56;
            Q56=makeQuery(id+"F0.imprint","IMPRINT",FACE,{"disambiguationData":[TD([[makeQuery(id+"F0.imprint","IMPRINT",EDGE,{"derivedFrom":sQuery(id+"F0.wireOp",EDGE,"E11.11.0.0")}),-1.0]])]});
            var Q57;
            Q57=makeQuery(id+"F0.imprint","IMPRINT",FACE,{"disambiguationData":[TD([[makeQuery(id+"F0.imprint","IMPRINT",EDGE,{"derivedFrom":sQuery(id+"F0.wireOp",EDGE,"E11.44.0.0")}),-1.0]])]});
            var Q58;
            Q58=makeQuery(id+"F0.imprint","IMPRINT",FACE,{"disambiguationData":[TD([[makeQuery(id+"F0.imprint","IMPRINT",EDGE,{"derivedFrom":sQuery(id+"F0.wireOp",EDGE,"E11.12.0.0")}),-1.0]])]});
            var Q59;
            Q59=makeQuery(id+"F0.imprint","IMPRINT",FACE,{"disambiguationData":[TD([[makeQuery(id+"F0.imprint","IMPRINT",EDGE,{"derivedFrom":sQuery(id+"F0.wireOp",EDGE,"E11.30.0.0")}),-1.0]])]});
            var Q60;
            Q60=makeQuery(id+"F0.imprint","IMPRINT",FACE,{"disambiguationData":[TD([[makeQuery(id+"F0.imprint","IMPRINT",EDGE,{"derivedFrom":sQuery(id+"F0.wireOp",EDGE,"E11.16.0.0")}),-1.0]])]});
            var Q61;
            Q61=makeQuery(id+"F0.imprint","IMPRINT",FACE,{"disambiguationData":[TD([[makeQuery(id+"F0.imprint","IMPRINT",EDGE,{"derivedFrom":sQuery(id+"F0.wireOp",EDGE,"E11.48.0.0")}),-1.0]])]});
            var Q62;
            Q62=makeQuery(id+"F0.imprint","IMPRINT",FACE,{"disambiguationData":[TD([[makeQuery(id+"F0.imprint","IMPRINT",EDGE,{"derivedFrom":sQuery(id+"F0.wireOp",EDGE,"E11.49.0.0")}),-1.0]])]});
            var Q63;
            Q63=makeQuery(id+"F0.imprint","IMPRINT",FACE,{"disambiguationData":[TD([[makeQuery(id+"F0.imprint","IMPRINT",EDGE,{"derivedFrom":sQuery(id+"F0.wireOp",EDGE,"E11.34.0.0")}),-1.0]])]});
            var Q64;
            Q64=makeQuery(id+"F0.imprint","IMPRINT",FACE,{"disambiguationData":[TD([[makeQuery(id+"F0.imprint","IMPRINT",EDGE,{"derivedFrom":sQuery(id+"F0.wireOp",EDGE,"E11.35.0.0")}),-1.0]])]});
            var Q65;
            Q65=makeQuery(id+"F0.imprint","IMPRINT",FACE,{"disambiguationData":[TD([[makeQuery(id+"F0.imprint","IMPRINT",EDGE,{"derivedFrom":sQuery(id+"F0.wireOp",EDGE,"E11.3.0.0")}),-1.0]])]});
            var Q66;
            Q66=makeQuery(id+"F0.imprint","IMPRINT",FACE,{"disambiguationData":[TD([[makeQuery(id+"F0.imprint","IMPRINT",EDGE,{"derivedFrom":sQuery(id+"F0.wireOp",EDGE,"E11.20.0.0")}),-1.0]])]});
            var Q67;
            Q67=makeQuery(id+"F0.imprint","IMPRINT",FACE,{"disambiguationData":[TD([[makeQuery(id+"F0.imprint","IMPRINT",EDGE,{"derivedFrom":sQuery(id+"F0.wireOp",EDGE,"E11.52.0.0")}),-1.0]])]});
            var Q68;
            Q68=makeQuery(id+"F0.imprint","IMPRINT",FACE,{"disambiguationData":[TD([[makeQuery(id+"F0.imprint","IMPRINT",EDGE,{"derivedFrom":sQuery(id+"F0.wireOp",EDGE,"E11.40.0.0")}),-1.0]])]});
            var Q69;
            Q69=makeQuery(id+"F0.imprint","IMPRINT",FACE,{"disambiguationData":[TD([[makeQuery(id+"F0.imprint","IMPRINT",EDGE,{"derivedFrom":sQuery(id+"F0.wireOp",EDGE,"E11.8.0.0")}),-1.0]])]});
            var Q70;
            Q70=makeQuery(id+"F0.imprint","IMPRINT",FACE,{"disambiguationData":[TD([[makeQuery(id+"F0.imprint","IMPRINT",EDGE,{"derivedFrom":sQuery(id+"F0.wireOp",EDGE,"E11.9.0.0")}),-1.0]])]});
            var Q71;
            Q71=makeQuery(id+"F0.imprint","IMPRINT",FACE,{"disambiguationData":[TD([[makeQuery(id+"F0.imprint","IMPRINT",EDGE,{"derivedFrom":sQuery(id+"F0.wireOp",EDGE,"E11.41.0.0")}),-1.0]])]});
            var Q72;
            Q72=makeQuery(id+"F0.imprint","IMPRINT",FACE,{"disambiguationData":[TD([[makeQuery(id+"F0.imprint","IMPRINT",EDGE,{"derivedFrom":sQuery(id+"F0.wireOp",EDGE,"E11.57.0.0")}),-1.0]])]});
            var Q73;
            Q73=makeQuery(id+"F0.imprint","IMPRINT",FACE,{"disambiguationData":[TD([[makeQuery(id+"F0.imprint","IMPRINT",EDGE,{"derivedFrom":sQuery(id+"F0.wireOp",EDGE,"E11.22.0.0")}),-1.0]])]});
            var Q74;
            Q74=makeQuery(id+"F0.imprint","IMPRINT",FACE,{"disambiguationData":[TD([[makeQuery(id+"F0.imprint","IMPRINT",EDGE,{"derivedFrom":sQuery(id+"F0.wireOp",EDGE,"E11.54.0.0")}),-1.0]])]});
            var Q75;
            Q75=makeQuery(id+"F0.imprint","IMPRINT",FACE,{"disambiguationData":[TD([[makeQuery(id+"F0.imprint","IMPRINT",EDGE,{"derivedFrom":sQuery(id+"F0.wireOp",EDGE,"E11.5.0.0")}),-1.0]])]});
            var Q76;
            Q76=makeQuery(id+"F0.imprint","IMPRINT",FACE,{"disambiguationData":[TD([[makeQuery(id+"F0.imprint","IMPRINT",EDGE,{"derivedFrom":sQuery(id+"F0.wireOp",EDGE,"E11.37.0.0")}),-1.0]])]});
            var Q77;
            Q77=makeQuery(id+"F0.imprint","IMPRINT",FACE,{"disambiguationData":[TD([[makeQuery(id+"F0.imprint","IMPRINT",EDGE,{"derivedFrom":sQuery(id+"F0.wireOp",EDGE,"E11.23.0.0")}),-1.0]])]});
            var Q78;
            Q78=makeQuery(id+"F0.imprint","IMPRINT",FACE,{"disambiguationData":[TD([[makeQuery(id+"F0.imprint","IMPRINT",EDGE,{"derivedFrom":sQuery(id+"F0.wireOp",EDGE,"E11.55.0.0")}),-1.0]])]});
            var Q79;
            Q79=makeQuery(id+"F0.imprint","IMPRINT",FACE,{"disambiguationData":[TD([[makeQuery(id+"F0.imprint","IMPRINT",EDGE,{"derivedFrom":sQuery(id+"F0.wireOp",EDGE,"E11.27.0.0")}),-1.0]])]});
            var Q80;
            Q80=makeQuery(id+"F0.imprint","IMPRINT",FACE,{"disambiguationData":[TD([[makeQuery(id+"F0.imprint","IMPRINT",EDGE,{"derivedFrom":sQuery(id+"F0.wireOp",EDGE,"E11.28.0.0")}),-1.0]])]});
            var Q81;
            Q81=makeQuery(id+"F0.imprint","IMPRINT",FACE,{"disambiguationData":[TD([[makeQuery(id+"F0.imprint","IMPRINT",EDGE,{"derivedFrom":sQuery(id+"F0.wireOp",EDGE,"E11.45.0.0")}),-1.0]])]});
            var Q82;
            Q82=makeQuery(id+"F0.imprint","IMPRINT",FACE,{"disambiguationData":[TD([[makeQuery(id+"F0.imprint","IMPRINT",EDGE,{"derivedFrom":sQuery(id+"F0.wireOp",EDGE,"E11.29.0.0")}),-1.0]])]});
            var Q83;
            Q83=makeQuery(id+"F0.imprint","IMPRINT",FACE,{"disambiguationData":[TD([[makeQuery(id+"F0.imprint","IMPRINT",EDGE,{"derivedFrom":sQuery(id+"F0.wireOp",EDGE,"E11.13.0.0")}),-1.0]])]});
            var Q84;
            Q84=makeQuery(id+"F0.imprint","IMPRINT",FACE,{"disambiguationData":[TD([[makeQuery(id+"F0.imprint","IMPRINT",EDGE,{"derivedFrom":sQuery(id+"F0.wireOp",EDGE,"E11.46.0.0")}),-1.0]])]});
            var Q85;
            Q85=makeQuery(id+"F0.imprint","IMPRINT",FACE,{"disambiguationData":[TD([[makeQuery(id+"F0.imprint","IMPRINT",EDGE,{"derivedFrom":sQuery(id+"F0.wireOp",EDGE,"E11.14.0.0")}),-1.0]])]});
            var Q86;
            Q86=makeQuery(id+"F0.imprint","IMPRINT",FACE,{"disambiguationData":[TD([[makeQuery(id+"F0.imprint","IMPRINT",EDGE,{"derivedFrom":sQuery(id+"F0.wireOp",EDGE,"E11.31.0.0")}),-1.0]])]});
            var Q87;
            Q87=makeQuery(id+"F0.imprint","IMPRINT",FACE,{"disambiguationData":[TD([[makeQuery(id+"F0.imprint","IMPRINT",EDGE,{"derivedFrom":sQuery(id+"F0.wireOp",EDGE,"E11.15.0.0")}),-1.0]])]});
            var Q88;
            Q88=makeQuery(id+"F0.imprint","IMPRINT",FACE,{"disambiguationData":[TD([[makeQuery(id+"F0.imprint","IMPRINT",EDGE,{"derivedFrom":sQuery(id+"F0.wireOp",EDGE,"E11.47.0.0")}),-1.0]])]});
            var Q89;
            Q89=makeQuery(id+"F0.imprint","IMPRINT",FACE,{"disambiguationData":[TD([[makeQuery(id+"F0.imprint","IMPRINT",EDGE,{"derivedFrom":sQuery(id+"F0.wireOp",EDGE,"E11.32.0.0")}),-1.0]])]});
            var Q90;
            Q90=makeQuery(id+"F0.imprint","IMPRINT",FACE,{"disambiguationData":[TD([[makeQuery(id+"F0.imprint","IMPRINT",EDGE,{"derivedFrom":sQuery(id+"F0.wireOp",EDGE,"E11.33.0.0")}),-1.0]])]});
            var Q91;
            Q91=makeQuery(id+"F0.imprint","IMPRINT",FACE,{"disambiguationData":[TD([[makeQuery(id+"F0.imprint","IMPRINT",EDGE,{"derivedFrom":sQuery(id+"F0.wireOp",EDGE,"E11.17.0.0")}),-1.0]])]});
            var Q92;
            Q92=makeQuery(id+"F0.imprint","IMPRINT",FACE,{"disambiguationData":[TD([[makeQuery(id+"F0.imprint","IMPRINT",EDGE,{"derivedFrom":sQuery(id+"F0.wireOp",EDGE,"E11.18.0.0")}),-1.0]])]});
            var Q93;
            Q93=makeQuery(id+"F0.imprint","IMPRINT",FACE,{"disambiguationData":[TD([[makeQuery(id+"F0.imprint","IMPRINT",EDGE,{"derivedFrom":sQuery(id+"F0.wireOp",EDGE,"E11.50.0.0")}),-1.0]])]});
            var Q94;
            Q94=makeQuery(id+"F0.imprint","IMPRINT",FACE,{"disambiguationData":[TD([[makeQuery(id+"F0.imprint","IMPRINT",EDGE,{"derivedFrom":sQuery(id+"F0.wireOp",EDGE,"E11.19.0.0")}),-1.0]])]});
            var Q95;
            Q95=makeQuery(id+"F0.imprint","IMPRINT",FACE,{"disambiguationData":[TD([[makeQuery(id+"F0.imprint","IMPRINT",EDGE,{"derivedFrom":sQuery(id+"F0.wireOp",EDGE,"E11.51.0.0")}),-1.0]])]});
            var Q96;
            Q96=makeQuery(id+"F0.imprint","IMPRINT",FACE,{"disambiguationData":[TD([[makeQuery(id+"F0.imprint","IMPRINT",EDGE,{"derivedFrom":sQuery(id+"F0.wireOp",EDGE,"E11.36.0.0")}),-1.0]])]});
            var Q97;
            Q97=makeQuery(id+"F0.imprint","IMPRINT",FACE,{"disambiguationData":[TD([[makeQuery(id+"F0.imprint","IMPRINT",EDGE,{"derivedFrom":sQuery(id+"F0.wireOp",EDGE,"E11.4.0.0")}),-1.0]])]});
            var Q98;
            {var subQ1=sQuery(id+"F0.wireOp",EDGE,"E9.0.7.0");Q98=makeQuery(id+"F0.imprint","IMPRINT",FACE,{"disambiguationData":[TD([[makeQuery(id+"F0.imprint","IMPRINT",EDGE,{"derivedFrom":subQ1}),-1.0]])]});}
            var Q99;
            {var subQ1=sQuery(id+"F0.wireOp",EDGE,"E9.0.6.0");Q99=makeQuery(id+"F0.imprint","IMPRINT",FACE,{"disambiguationData":[TD([[makeQuery(id+"F0.imprint","IMPRINT",EDGE,{"derivedFrom":subQ1}),-1.0]])]});}
            var Q100;
            {var subQ1=sQuery(id+"F0.wireOp",EDGE,"E9.0.4.0");Q100=makeQuery(id+"F0.imprint","IMPRINT",FACE,{"disambiguationData":[TD([[makeQuery(id+"F0.imprint","IMPRINT",EDGE,{"derivedFrom":subQ1}),-1.0]])]});}
            var Q101;
            {var subQ1=sQuery(id+"F0.wireOp",EDGE,"E9.0.3.0");Q101=makeQuery(id+"F0.imprint","IMPRINT",FACE,{"disambiguationData":[TD([[makeQuery(id+"F0.imprint","IMPRINT",EDGE,{"derivedFrom":subQ1}),-1.0]])]});}
            var Q102;
            {var subQ1=sQuery(id+"F0.wireOp",EDGE,"E9.0.2.0");Q102=makeQuery(id+"F0.imprint","IMPRINT",FACE,{"disambiguationData":[TD([[makeQuery(id+"F0.imprint","IMPRINT",EDGE,{"derivedFrom":subQ1}),-1.0]])]});}
            var Q103;
            {var subQ1=sQuery(id+"F0.wireOp",EDGE,"E9.0.10.0");Q103=makeQuery(id+"F0.imprint","IMPRINT",FACE,{"disambiguationData":[TD([[makeQuery(id+"F0.imprint","IMPRINT",EDGE,{"derivedFrom":subQ1}),-1.0]])]});}
            var Q104;
            {var subQ1=sQuery(id+"F0.wireOp",EDGE,"E9.0.9.0");Q104=makeQuery(id+"F0.imprint","IMPRINT",FACE,{"disambiguationData":[TD([[makeQuery(id+"F0.imprint","IMPRINT",EDGE,{"derivedFrom":subQ1}),-1.0]])]});}
            var Q105;
            {var subQ1=sQuery(id+"F0.wireOp",EDGE,"E9.0.14.0");Q105=makeQuery(id+"F0.imprint","IMPRINT",FACE,{"disambiguationData":[TD([[makeQuery(id+"F0.imprint","IMPRINT",EDGE,{"derivedFrom":subQ1}),-1.0]])]});}
            var Q106;
            {var subQ1=sQuery(id+"F0.wireOp",EDGE,"E9.0.12.0");Q106=makeQuery(id+"F0.imprint","IMPRINT",FACE,{"disambiguationData":[TD([[makeQuery(id+"F0.imprint","IMPRINT",EDGE,{"derivedFrom":subQ1}),-1.0]])]});}
            var Q107;
            {var subQ1=sQuery(id+"F0.wireOp",EDGE,"E9.0.11.0");Q107=makeQuery(id+"F0.imprint","IMPRINT",FACE,{"disambiguationData":[TD([[makeQuery(id+"F0.imprint","IMPRINT",EDGE,{"derivedFrom":subQ1}),-1.0]])]});}
            var Q108;
            {var subQ1=sQuery(id+"F0.wireOp",EDGE,"E9.0.5.0");Q108=makeQuery(id+"F0.imprint","IMPRINT",FACE,{"disambiguationData":[TD([[makeQuery(id+"F0.imprint","IMPRINT",EDGE,{"derivedFrom":subQ1}),-1.0]])]});}
            var Q109;
            {var subQ1=sQuery(id+"F0.wireOp",EDGE,"E9.0.1.0");Q109=makeQuery(id+"F0.imprint","IMPRINT",FACE,{"disambiguationData":[TD([[makeQuery(id+"F0.imprint","IMPRINT",EDGE,{"derivedFrom":subQ1}),-1.0]])]});}
            var Q110;
            {var subQ1=sQuery(id+"F0.wireOp",EDGE,"E9.0.8.0");Q110=makeQuery(id+"F0.imprint","IMPRINT",FACE,{"disambiguationData":[TD([[makeQuery(id+"F0.imprint","IMPRINT",EDGE,{"derivedFrom":subQ1}),-1.0]])]});}
            var Q111;
            {var subQ1=sQuery(id+"F0.wireOp",EDGE,"E9.0.13.0");Q111=makeQuery(id+"F0.imprint","IMPRINT",FACE,{"disambiguationData":[TD([[makeQuery(id+"F0.imprint","IMPRINT",EDGE,{"derivedFrom":subQ1}),-1.0]])]});}
            var Q112;
            Q112=makeQuery(id+"F0.imprint","IMPRINT",FACE,{"disambiguationData":[TD([[makeQuery(id+"F0.imprint","IMPRINT",EDGE,{"derivedFrom":sQuery(id+"F0.wireOp",EDGE,"E8.bottom")}),1.0]])]});
            var Q113;
            {var subQ1=sQuery(id+"F0.wireOp",EDGE,"E9.0.22.0");Q113=makeQuery(id+"F0.imprint","IMPRINT",FACE,{"disambiguationData":[TD([[makeQuery(id+"F0.imprint","IMPRINT",EDGE,{"derivedFrom":subQ1}),-1.0]])]});}
            var Q114;
            {var subQ1=sQuery(id+"F0.wireOp",EDGE,"E9.0.21.0");Q114=makeQuery(id+"F0.imprint","IMPRINT",FACE,{"disambiguationData":[TD([[makeQuery(id+"F0.imprint","IMPRINT",EDGE,{"derivedFrom":subQ1}),-1.0]])]});}
            var Q115;
            {var subQ1=sQuery(id+"F0.wireOp",EDGE,"E9.0.20.0");Q115=makeQuery(id+"F0.imprint","IMPRINT",FACE,{"disambiguationData":[TD([[makeQuery(id+"F0.imprint","IMPRINT",EDGE,{"derivedFrom":subQ1}),-1.0]])]});}
            var Q116;
            {var subQ1=sQuery(id+"F0.wireOp",EDGE,"E9.0.16.0");Q116=makeQuery(id+"F0.imprint","IMPRINT",FACE,{"disambiguationData":[TD([[makeQuery(id+"F0.imprint","IMPRINT",EDGE,{"derivedFrom":subQ1}),-1.0]])]});}
            var Q117;
            {var subQ1=sQuery(id+"F0.wireOp",EDGE,"E9.0.19.0");Q117=makeQuery(id+"F0.imprint","IMPRINT",FACE,{"disambiguationData":[TD([[makeQuery(id+"F0.imprint","IMPRINT",EDGE,{"derivedFrom":subQ1}),-1.0]])]});}
            var Q118;
            {var subQ1=sQuery(id+"F0.wireOp",EDGE,"E9.0.18.0");Q118=makeQuery(id+"F0.imprint","IMPRINT",FACE,{"disambiguationData":[TD([[makeQuery(id+"F0.imprint","IMPRINT",EDGE,{"derivedFrom":subQ1}),-1.0]])]});}
            var Q119;
            {var subQ1=sQuery(id+"F0.wireOp",EDGE,"E9.0.17.0");Q119=makeQuery(id+"F0.imprint","IMPRINT",FACE,{"disambiguationData":[TD([[makeQuery(id+"F0.imprint","IMPRINT",EDGE,{"derivedFrom":subQ1}),-1.0]])]});}
            var Q120;
            {var subQ1=sQuery(id+"F0.wireOp",EDGE,"E9.0.15.0");Q120=makeQuery(id+"F0.imprint","IMPRINT",FACE,{"disambiguationData":[TD([[makeQuery(id+"F0.imprint","IMPRINT",EDGE,{"derivedFrom":subQ1}),-1.0]])]});}
            var Q121;
            Q121=makeQuery(id+"F0.imprint","IMPRINT",FACE,{"disambiguationData":[TD([[makeQuery(id+"F0.imprint","IMPRINT",EDGE,{"derivedFrom":sQuery(id+"F0.wireOp",EDGE,"E10.bottom")}),-1.0]])]});
            var Q122;
            Q122=makeQuery(id+"F0.imprint","IMPRINT",FACE,{"disambiguationData":[TD([[makeQuery(id+"F0.imprint","IMPRINT",EDGE,{"derivedFrom":sQuery(id+"F0.wireOp",EDGE,"E11.1.0.0")}),-1.0]])]});
            var Q123;
            {var subQ1=sQuery(id+"F0.wireOp",EDGE,"E9.0.23.0");Q123=makeQuery(id+"F0.imprint","IMPRINT",FACE,{"disambiguationData":[TD([[makeQuery(id+"F0.imprint","IMPRINT",EDGE,{"derivedFrom":subQ1}),-1.0]])]});}
            var Q124;
            Q124=makeQuery(id+"F0.imprint","IMPRINT",FACE,{"disambiguationData":[TD([[makeQuery(id+"F0.imprint","IMPRINT",EDGE,{"derivedFrom":sQuery(id+"F0.wireOp",EDGE,"E11.2.0.0")}),-1.0]])]});
            var Q125;
            Q125=sQuery(id+"F0.wireOp",EDGE,"E11.56.0.3");
            var Q126;
            Q126=sQuery(id+"F0.wireOp",EDGE,"E11.65.0.0");
            var Q127;
            Q127=sQuery(id+"F0.wireOp",EDGE,"E11.64.0.3");
            var Q128;
            Q128=sQuery(id+"F0.wireOp",EDGE,"E11.65.0.1");
            var Q129;
            Q129=sQuery(id+"F0.wireOp",EDGE,"E12.0.73.0");
            var Q130;
            Q130=sQuery(id+"F0.wireOp",EDGE,"E11.44.0.3");
            var Q131;
            Q131=sQuery(id+"F0.wireOp",EDGE,"E11.48.0.3");
            var Q132;
            Q132=sQuery(id+"F0.wireOp",EDGE,"E11.56.0.2");
            var Q133;
            Q133=sQuery(id+"F0.wireOp",EDGE,"E11.64.0.2");
            var Q134;
            Q134=sQuery(id+"F0.wireOp",EDGE,"E11.44.0.2");
            var Q135;
            Q135=sQuery(id+"F0.wireOp",EDGE,"E11.48.0.2");
            var Q136;
            Q136=sQuery(id+"F0.wireOp",EDGE,"E11.56.0.1");
            var Q137;
            Q137=sQuery(id+"F0.wireOp",EDGE,"E11.48.0.1");
            var Q138;
            Q138=sQuery(id+"F0.wireOp",EDGE,"E11.56.0.0");
            var Q139;
            Q139=sQuery(id+"F0.wireOp",EDGE,"E11.63.0.3");
            var Q140;
            Q140=sQuery(id+"F0.wireOp",EDGE,"E11.63.0.2");
            var Q141;
            Q141=sQuery(id+"F0.wireOp",EDGE,"E11.43.0.0");
            var Q142;
            Q142=sQuery(id+"F0.wireOp",EDGE,"E11.54.0.3");
            var Q143;
            Q143=sQuery(id+"F0.wireOp",EDGE,"E11.46.0.3");
            var Q144;
            Q144=sQuery(id+"F0.wireOp",EDGE,"E11.54.0.2");
            var Q145;
            Q145=sQuery(id+"F0.wireOp",EDGE,"E11.46.0.2");
            var Q146;
            Q146=sQuery(id+"F0.wireOp",EDGE,"E11.53.0.2");
            var Q147;
            Q147=sQuery(id+"F0.wireOp",EDGE,"E11.53.0.3");
            var Q148;
            Q148=sQuery(id+"F0.wireOp",EDGE,"E12.6.73.0");
            var Q149;
            Q149=sQuery(id+"F0.wireOp",EDGE,"E11.65.0.3");
            var Q150;
            Q150=sQuery(id+"F0.wireOp",EDGE,"E11.58.0.0");
            var Q151;
            Q151=sQuery(id+"F0.wireOp",EDGE,"E11.54.0.0");
            var Q152;
            Q152=sQuery(id+"F0.wireOp",EDGE,"E11.46.0.0");
            var Q153;
            Q153=sQuery(id+"F0.wireOp",EDGE,"E12.9.73.0");
            var Q154;
            Q154=sQuery(id+"F0.wireOp",EDGE,"E11.58.0.1");
            var Q155;
            Q155=sQuery(id+"F0.wireOp",EDGE,"E11.54.0.1");
            var Q156;
            Q156=sQuery(id+"F0.wireOp",EDGE,"E11.46.0.1");
            var Q157;
            Q157=sQuery(id+"F0.wireOp",EDGE,"E15.0.15.3");
            var Q158;
            Q158=sQuery(id+"F0.wireOp",EDGE,"E15.0.7.3");
            var Q159;
            Q159=sQuery(id+"F0.wireOp",EDGE,"E15.0.11.3");
            var Q160;
            Q160=sQuery(id+"F0.wireOp",EDGE,"E15.0.19.3");
            var Q161;
            Q161=sQuery(id+"F0.wireOp",EDGE,"E12.6.68.0");
            var Q162;
            Q162=sQuery(id+"F0.wireOp",EDGE,"E15.0.3.2");
            var Q163;
            Q163=sQuery(id+"F0.wireOp",EDGE,"E15.0.3.3");
            var Q164;
            Q164=sQuery(id+"F0.wireOp",EDGE,"E11.61.0.0");
            var Q165;
            Q165=sQuery(id+"F0.wireOp",EDGE,"E12.9.68.0");
            var Q166;
            Q166=sQuery(id+"F0.wireOp",EDGE,"E15.0.16.0");
            var Q167;
            Q167=sQuery(id+"F0.wireOp",EDGE,"E15.0.12.0");
            var Q168;
            Q168=sQuery(id+"F0.wireOp",EDGE,"E15.0.4.0");
            var Q169;
            Q169=sQuery(id+"F0.wireOp",EDGE,"E11.61.0.1");
            var Q170;
            Q170=sQuery(id+"F0.wireOp",EDGE,"E11.53.0.1");
            var Q171;
            Q171=sQuery(id+"F0.wireOp",EDGE,"E11.53.0.0");
            var Q172;
            Q172=sQuery(id+"F0.wireOp",EDGE,"E15.0.15.2");
            var Q173;
            Q173=sQuery(id+"F0.wireOp",EDGE,"E15.0.19.2");
            var Q174;
            Q174=sQuery(id+"F0.wireOp",EDGE,"E15.0.7.2");
            var Q175;
            Q175=sQuery(id+"F0.wireOp",EDGE,"E15.0.11.2");
            var Q176;
            Q176=sQuery(id+"F0.wireOp",EDGE,"E15.0.11.1");
            var Q177;
            Q177=sQuery(id+"F0.wireOp",EDGE,"E15.0.7.1");
            var Q178;
            Q178=sQuery(id+"F0.wireOp",EDGE,"E11.64.0.1");
            var Q179;
            Q179=sQuery(id+"F0.wireOp",EDGE,"E11.44.0.1");
            var Q180;
            Q180=sQuery(id+"F0.wireOp",EDGE,"E15.0.15.0");
            var Q181;
            Q181=sQuery(id+"F0.wireOp",EDGE,"E15.0.7.0");
            var Q182;
            Q182=sQuery(id+"F0.wireOp",EDGE,"E15.0.11.0");
            var Q183;
            Q183=sQuery(id+"F0.wireOp",EDGE,"E12.0.68.0");
            var Q184;
            Q184=sQuery(id+"F0.wireOp",EDGE,"E11.44.0.0");
            var Q185;
            Q185=sQuery(id+"F0.wireOp",EDGE,"E11.48.0.0");
            var Q186;
            Q186=sQuery(id+"F0.wireOp",EDGE,"E15.0.14.3");
            var Q187;
            Q187=sQuery(id+"F0.wireOp",EDGE,"E15.0.10.3");
            var Q188;
            Q188=sQuery(id+"F0.wireOp",EDGE,"E15.0.2.3");
            var Q189;
            Q189=sQuery(id+"F0.wireOp",EDGE,"E11.64.0.0");
            var Q190;
            Q190=sQuery(id+"F0.wireOp",EDGE,"E15.0.10.2");
            var Q191;
            Q191=sQuery(id+"F0.wireOp",EDGE,"E15.0.2.2");
            var Q192;
            Q192=sQuery(id+"F0.wireOp",EDGE,"E11.51.0.3");
            var Q193;
            Q193=sQuery(id+"F0.wireOp",EDGE,"E11.59.0.3");
            var Q194;
            Q194=sQuery(id+"F0.wireOp",EDGE,"E15.0.14.1");
            var Q195;
            Q195=sQuery(id+"F0.wireOp",EDGE,"E15.0.6.1");
            var Q196;
            Q196=sQuery(id+"F0.wireOp",EDGE,"E15.0.10.1");
            var Q197;
            Q197=sQuery(id+"F0.wireOp",EDGE,"E11.51.0.2");
            var Q198;
            Q198=sQuery(id+"F0.wireOp",EDGE,"E15.0.2.1");
            var Q199;
            Q199=sQuery(id+"F0.wireOp",EDGE,"E11.59.0.2");
            var Q200;
            Q200=sQuery(id+"F0.wireOp",EDGE,"E15.0.10.0");
            var Q201;
            Q201=sQuery(id+"F0.wireOp",EDGE,"E15.0.2.0");
            var Q202;
            Q202=sQuery(id+"F0.wireOp",EDGE,"E11.51.0.1");
            var Q203;
            Q203=sQuery(id+"F0.wireOp",EDGE,"E11.63.0.1");
            var Q204;
            Q204=sQuery(id+"F0.wireOp",EDGE,"E12.9.70.0");
            var Q205;
            Q205=sQuery(id+"F0.wireOp",EDGE,"E12.9.74.0");
            var Q206;
            Q206=sQuery(id+"F0.wireOp",EDGE,"E11.51.0.0");
            var Q207;
            Q207=sQuery(id+"F0.wireOp",EDGE,"E11.63.0.0");
            var Q208;
            Q208=sQuery(id+"F0.wireOp",EDGE,"E15.0.9.3");
            var Q209;
            Q209=sQuery(id+"F0.wireOp",EDGE,"E12.6.70.0");
            var Q210;
            Q210=sQuery(id+"F0.wireOp",EDGE,"E12.6.74.0");
            var Q211;
            Q211=sQuery(id+"F0.wireOp",EDGE,"E15.0.1.2");
            var Q212;
            Q212=sQuery(id+"F0.wireOp",EDGE,"E11.58.0.3");
            var Q213;
            Q213=sQuery(id+"F0.wireOp",EDGE,"E15.0.21.2");
            var Q214;
            Q214=sQuery(id+"F0.wireOp",EDGE,"E15.0.9.2");
            var Q215;
            Q215=sQuery(id+"F0.wireOp",EDGE,"E11.58.0.2");
            var Q216;
            Q216=sQuery(id+"F0.wireOp",EDGE,"E15.0.9.1");
            var Q217;
            Q217=sQuery(id+"F0.wireOp",EDGE,"E12.3.70.0");
            var Q218;
            Q218=sQuery(id+"F0.wireOp",EDGE,"E15.0.1.1");
            var Q219;
            Q219=sQuery(id+"F0.wireOp",EDGE,"E11.49.0.2");
            var Q220;
            Q220=sQuery(id+"F0.wireOp",EDGE,"E12.3.73.0");
            var Q221;
            Q221=sQuery(id+"F0.wireOp",EDGE,"E11.65.0.2");
            var Q222;
            Q222=sQuery(id+"F0.wireOp",EDGE,"E11.61.0.2");
            var Q223;
            Q223=sQuery(id+"F0.wireOp",EDGE,"E15.0.4.1");
            var Q224;
            Q224=sQuery(id+"F0.wireOp",EDGE,"E15.0.8.1");
            var Q225;
            Q225=sQuery(id+"F0.wireOp",EDGE,"E11.49.0.3");
            var Q226;
            Q226=sQuery(id+"F0.wireOp",EDGE,"E12.6.69.0");
            var Q227;
            Q227=sQuery(id+"F0.wireOp",EDGE,"E11.61.0.3");
            var Q228;
            Q228=sQuery(id+"F0.wireOp",EDGE,"E15.0.4.2");
            var Q229;
            Q229=sQuery(id+"F0.wireOp",EDGE,"E15.0.20.2");
            var Q230;
            Q230=sQuery(id+"F0.wireOp",EDGE,"E15.0.8.2");
            var Q231;
            Q231=sQuery(id+"F0.wireOp",EDGE,"E12.9.69.0");
            var Q232;
            Q232=sQuery(id+"F0.wireOp",EDGE,"E15.0.4.3");
            var Q233;
            Q233=sQuery(id+"F0.wireOp",EDGE,"E15.0.20.3");
            var Q234;
            Q234=sQuery(id+"F0.wireOp",EDGE,"E15.0.12.3");
            var Q235;
            Q235=sQuery(id+"F0.wireOp",EDGE,"E15.0.8.3");
            var Q236;
            Q236=sQuery(id+"F0.wireOp",EDGE,"E12.0.74.0");
            var Q237;
            Q237=sQuery(id+"F0.wireOp",EDGE,"E12.0.70.0");
            var Q238;
            Q238=sQuery(id+"F0.wireOp",EDGE,"E15.0.21.0");
            var Q239;
            Q239=sQuery(id+"F0.wireOp",EDGE,"E15.0.9.0");
            var Q240;
            Q240=sQuery(id+"F0.wireOp",EDGE,"E12.6.72.0");
            var Q241;
            Q241=sQuery(id+"F0.wireOp",EDGE,"E11.52.0.3");
            var Q242;
            Q242=sQuery(id+"F0.wireOp",EDGE,"E11.60.0.3");
            var Q243;
            Q243=sQuery(id+"F0.wireOp",EDGE,"E12.9.72.0");
            var Q244;
            Q244=sQuery(id+"F0.wireOp",EDGE,"E11.49.0.0");
            var Q245;
            Q245=sQuery(id+"F0.wireOp",EDGE,"E15.0.8.0");
            var Q246;
            Q246=sQuery(id+"F0.wireOp",EDGE,"E15.0.20.0");
            var Q247;
            Q247=sQuery(id+"F0.wireOp",EDGE,"E12.0.69.0");
            var Q248;
            Q248=sQuery(id+"F0.wireOp",EDGE,"E11.45.0.1");
            var Q249;
            Q249=sQuery(id+"F0.wireOp",EDGE,"E11.49.0.1");
            var Q250;
            Q250=sQuery(id+"F0.wireOp",EDGE,"E11.57.0.1");
            var Q251;
            Q251=sQuery(id+"F0.wireOp",EDGE,"E11.57.0.0");
            var Q252;
            Q252=sQuery(id+"F0.wireOp",EDGE,"E12.3.68.0");
            var Q253;
            Q253=sQuery(id+"F0.wireOp",EDGE,"E15.0.3.1");
            var Q254;
            Q254=sQuery(id+"F0.wireOp",EDGE,"E11.52.0.2");
            var Q255;
            Q255=sQuery(id+"F0.wireOp",EDGE,"E15.0.19.1");
            var Q256;
            Q256=sQuery(id+"F0.wireOp",EDGE,"E15.0.15.1");
            var Q257;
            Q257=sQuery(id+"F0.wireOp",EDGE,"E11.52.0.1");
            var Q258;
            Q258=sQuery(id+"F0.wireOp",EDGE,"E11.60.0.1");
            var Q259;
            Q259=sQuery(id+"F0.wireOp",EDGE,"E15.0.19.0");
            var Q260;
            Q260=sQuery(id+"F0.wireOp",EDGE,"E12.0.72.0");
            var Q261;
            Q261=sQuery(id+"F0.wireOp",EDGE,"E15.0.3.0");
            var Q262;
            Q262=sQuery(id+"F0.wireOp",EDGE,"E15.0.18.3");
            var Q263;
            Q263=sQuery(id+"F0.wireOp",EDGE,"E15.0.22.3");
            var Q264;
            Q264=sQuery(id+"F0.wireOp",EDGE,"E15.0.6.3");
            var Q265;
            Q265=sQuery(id+"F0.wireOp",EDGE,"E12.9.71.0");
            var Q266;
            Q266=sQuery(id+"F0.wireOp",EDGE,"E11.52.0.0");
            var Q267;
            Q267=sQuery(id+"F0.wireOp",EDGE,"E11.60.0.0");
            var Q268;
            Q268=sQuery(id+"F0.wireOp",EDGE,"E15.0.14.2");
            var Q269;
            Q269=sQuery(id+"F0.wireOp",EDGE,"E15.0.22.2");
            var Q270;
            Q270=sQuery(id+"F0.wireOp",EDGE,"E15.0.18.2");
            var Q271;
            Q271=sQuery(id+"F0.wireOp",EDGE,"E15.0.6.2");
            var Q272;
            Q272=sQuery(id+"F0.wireOp",EDGE,"E11.67.0.3");
            var Q273;
            Q273=sQuery(id+"F0.wireOp",EDGE,"E12.6.71.0");
            var Q274;
            Q274=sQuery(id+"F0.wireOp",EDGE,"E11.55.0.3");
            var Q275;
            Q275=sQuery(id+"F0.wireOp",EDGE,"E11.47.0.3");
            var Q276;
            Q276=sQuery(id+"F0.wireOp",EDGE,"E15.0.22.1");
            var Q277;
            Q277=sQuery(id+"F0.wireOp",EDGE,"E15.0.18.1");
            var Q278;
            Q278=sQuery(id+"F0.wireOp",EDGE,"E11.67.0.2");
            var Q279;
            Q279=sQuery(id+"F0.wireOp",EDGE,"E12.3.71.0");
            var Q280;
            Q280=sQuery(id+"F0.wireOp",EDGE,"E12.3.75.0");
            var Q281;
            Q281=sQuery(id+"F0.wireOp",EDGE,"E11.47.0.2");
            var Q282;
            Q282=sQuery(id+"F0.wireOp",EDGE,"E15.0.14.0");
            var Q283;
            Q283=sQuery(id+"F0.wireOp",EDGE,"E15.0.18.0");
            var Q284;
            Q284=sQuery(id+"F0.wireOp",EDGE,"E15.0.22.0");
            var Q285;
            Q285=sQuery(id+"F0.wireOp",EDGE,"E15.0.6.0");
            var Q286;
            Q286=sQuery(id+"F0.wireOp",EDGE,"E12.0.71.0");
            var Q287;
            Q287=sQuery(id+"F0.wireOp",EDGE,"E11.55.0.1");
            var Q288;
            Q288=sQuery(id+"F0.wireOp",EDGE,"E11.59.0.1");
            var Q289;
            Q289=sQuery(id+"F0.wireOp",EDGE,"E11.47.0.1");
            var Q290;
            Q290=sQuery(id+"F0.wireOp",EDGE,"E15.0.5.3");
            var Q291;
            Q291=sQuery(id+"F0.wireOp",EDGE,"E11.67.0.0");
            var Q292;
            Q292=sQuery(id+"F0.wireOp",EDGE,"E11.59.0.0");
            var Q293;
            Q293=sQuery(id+"F0.wireOp",EDGE,"E11.47.0.0");
            var Q294;
            Q294=sQuery(id+"F0.wireOp",EDGE,"E15.0.13.3");
            var Q295;
            Q295=sQuery(id+"F0.wireOp",EDGE,"E15.0.17.3");
            var Q296;
            Q296=sQuery(id+"F0.wireOp",EDGE,"E15.0.21.3");
            var Q297;
            Q297=sQuery(id+"F0.wireOp",EDGE,"E11.66.0.3");
            var Q298;
            Q298=sQuery(id+"F0.wireOp",EDGE,"E11.50.0.3");
            var Q299;
            Q299=sQuery(id+"F0.wireOp",EDGE,"E11.62.0.3");
            var Q300;
            Q300=sQuery(id+"F0.wireOp",EDGE,"E15.0.13.2");
            var Q301;
            Q301=sQuery(id+"F0.wireOp",EDGE,"E15.0.17.2");
            var Q302;
            Q302=sQuery(id+"F0.wireOp",EDGE,"E15.0.5.2");
            var Q303;
            Q303=sQuery(id+"F0.wireOp",EDGE,"E11.50.0.2");
            var Q304;
            Q304=sQuery(id+"F0.wireOp",EDGE,"E11.62.0.2");
            var Q305;
            Q305=sQuery(id+"F0.wireOp",EDGE,"E15.0.13.1");
            var Q306;
            Q306=sQuery(id+"F0.wireOp",EDGE,"E15.0.17.1");
            var Q307;
            Q307=sQuery(id+"F0.wireOp",EDGE,"E15.0.21.1");
            var Q308;
            Q308=sQuery(id+"F0.wireOp",EDGE,"E11.66.0.2");
            var Q309;
            Q309=sQuery(id+"F0.wireOp",EDGE,"E12.3.74.0");
            var Q310;
            Q310=sQuery(id+"F0.wireOp",EDGE,"E11.57.0.2");
            var Q311;
            Q311=sQuery(id+"F0.wireOp",EDGE,"E11.45.0.2");
            var Q312;
            Q312=sQuery(id+"F0.wireOp",EDGE,"E12.3.69.0");
            var Q313;
            Q313=sQuery(id+"F0.wireOp",EDGE,"E15.0.20.1");
            var Q314;
            Q314=sQuery(id+"F0.wireOp",EDGE,"E15.0.16.1");
            var Q315;
            Q315=sQuery(id+"F0.wireOp",EDGE,"E15.0.12.1");
            var Q316;
            Q316=sQuery(id+"F0.wireOp",EDGE,"E11.57.0.3");
            var Q317;
            Q317=sQuery(id+"F0.wireOp",EDGE,"E11.45.0.3");
            var Q318;
            Q318=sQuery(id+"F0.wireOp",EDGE,"E15.0.16.2");
            var Q319;
            Q319=sQuery(id+"F0.wireOp",EDGE,"E15.0.12.2");
            var Q320;
            Q320=sQuery(id+"F0.wireOp",EDGE,"E11.50.0.0");
            var Q321;
            Q321=sQuery(id+"F0.wireOp",EDGE,"E11.66.0.0");
            var Q322;
            Q322=sQuery(id+"F0.wireOp",EDGE,"E11.62.0.0");
            var Q323;
            Q323=sQuery(id+"F0.wireOp",EDGE,"E15.0.16.3");
            var Q324;
            Q324=sQuery(id+"F0.wireOp",EDGE,"E11.50.0.1");
            var Q325;
            Q325=sQuery(id+"F0.wireOp",EDGE,"E11.66.0.1");
            var Q326;
            Q326=sQuery(id+"F0.wireOp",EDGE,"E11.62.0.1");
            var Q327;
            Q327=sQuery(id+"F0.wireOp",EDGE,"E15.0.5.0");
            var Q328;
            Q328=sQuery(id+"F0.wireOp",EDGE,"E15.0.1.0");
            var Q329;
            Q329=sQuery(id+"F0.wireOp",EDGE,"E15.0.17.0");
            var Q330;
            Q330=sQuery(id+"F0.wireOp",EDGE,"E15.0.13.0");
            var Q331;
            Q331=sQuery(id+"F0.wireOp",EDGE,"E15.0.23.3");
            var Q332;
            Q332=sQuery(id+"F0.wireOp",EDGE,"E11.45.0.0");
            var Q333;
            Q333=sQuery(id+"F0.wireOp",EDGE,"E12.3.72.0");
            var Q334;
            Q334=sQuery(id+"F0.wireOp",EDGE,"E11.60.0.2");
            var Q335;
            Q335=sQuery(id+"F0.wireOp",EDGE,"E15.0.23.0");
            var Q336;
            Q336=sQuery(id+"F0.wireOp",EDGE,"E12.9.75.0");
            var Q337;
            Q337=sQuery(id+"F0.wireOp",EDGE,"E12.6.75.0");
            var Q338;
            Q338=sQuery(id+"F0.wireOp",EDGE,"E11.55.0.2");
            var Q339;
            Q339=sQuery(id+"F0.wireOp",EDGE,"E11.67.0.1");
            var Q340;
            Q340=sQuery(id+"F0.wireOp",EDGE,"E12.0.75.0");
            var Q341;
            Q341=sQuery(id+"F0.wireOp",EDGE,"E11.55.0.0");
            var Q342;
            Q342=sQuery(id+"F0.wireOp",EDGE,"E15.0.5.1");
            var Q343;
            Q343=sQuery(id+"F0.wireOp",EDGE,"E13.left");
            var Q344;
            Q344=sQuery(id+"F0.wireOp",EDGE,"E13.right");
            var Q345;
            Q345=sQuery(id+"F0.wireOp",EDGE,"E15.0.23.2");
            var Q346;
            Q346=sQuery(id+"F0.wireOp",EDGE,"E13.top");
            var Q347;
            Q347=sQuery(id+"F0.wireOp",EDGE,"E15.0.23.1");
            var Q348;
            Q348=sQuery(id+"F0.wireOp",EDGE,"E13.bottom");
            var Q349;
            Q349=sQuery(id+"F0.wireOp",EDGE,"E15.0.1.3");
            var Q350;
            Q350=sQuery(id+"F0.wireOp",EDGE,"E14.top");
            var Q351;
            Q351=sQuery(id+"F0.wireOp",EDGE,"E14.left");
            var Q352;
            Q352=sQuery(id+"F0.wireOp",EDGE,"E14.bottom");
            var Q353;
            Q353=sQuery(id+"F0.wireOp",EDGE,"E14.right");
            var Q354;
            Q354=sQuery(id+"F0.wireOp",EDGE,"E9.0.10.2");
            var Q355;
            Q355=sQuery(id+"F0.wireOp",EDGE,"E11.41.0.1");
            var Q356;
            Q356=sQuery(id+"F0.wireOp",EDGE,"E9.0.9.2");
            var Q357;
            Q357=sQuery(id+"F0.wireOp",EDGE,"E9.0.15.0");
            var Q358;
            Q358=sQuery(id+"F0.wireOp",EDGE,"E9.0.20.1");
            var Q359;
            Q359=sQuery(id+"F0.wireOp",EDGE,"E9.0.4.1");
            var Q360;
            Q360=sQuery(id+"F0.wireOp",EDGE,"E11.21.0.1");
            var Q361;
            Q361=sQuery(id+"F0.wireOp",EDGE,"E9.0.10.0");
            var Q362;
            Q362=sQuery(id+"F0.wireOp",EDGE,"E9.0.15.1");
            var Q363;
            Q363=sQuery(id+"F0.wireOp",EDGE,"E9.0.5.1");
            var Q364;
            Q364=sQuery(id+"F0.wireOp",EDGE,"E9.0.15.2");
            var Q365;
            Q365=sQuery(id+"F0.wireOp",EDGE,"E9.0.10.1");
            var Q366;
            Q366=sQuery(id+"F0.wireOp",EDGE,"E9.0.5.0");
            var Q367;
            Q367=sQuery(id+"F0.wireOp",EDGE,"E9.0.14.2");
            var Q368;
            Q368=sQuery(id+"F0.wireOp",EDGE,"E9.0.19.2");
            var Q369;
            Q369=sQuery(id+"F0.wireOp",EDGE,"E9.0.3.2");
            var Q370;
            Q370=sQuery(id+"F0.wireOp",EDGE,"E11.36.0.0");
            var Q371;
            Q371=sQuery(id+"F0.wireOp",EDGE,"E9.0.3.1");
            var Q372;
            Q372=sQuery(id+"F0.wireOp",EDGE,"E9.0.8.1");
            var Q373;
            Q373=sQuery(id+"F0.wireOp",EDGE,"E9.0.19.0");
            var Q374;
            Q374=sQuery(id+"F0.wireOp",EDGE,"E11.7.0.2");
            var Q375;
            Q375=sQuery(id+"F0.wireOp",EDGE,"E9.0.8.0");
            var Q376;
            Q376=sQuery(id+"F0.wireOp",EDGE,"E9.0.13.1");
            var Q377;
            Q377=sQuery(id+"F0.wireOp",EDGE,"E9.0.2.2");
            var Q378;
            Q378=sQuery(id+"F0.wireOp",EDGE,"E9.0.7.2");
            var Q379;
            Q379=sQuery(id+"F0.wireOp",EDGE,"E9.0.13.0");
            var Q380;
            Q380=sQuery(id+"F0.wireOp",EDGE,"E9.0.18.1");
            var Q381;
            Q381=sQuery(id+"F0.wireOp",EDGE,"E11.31.0.1");
            var Q382;
            Q382=sQuery(id+"F0.wireOp",EDGE,"E11.7.0.0");
            var Q383;
            Q383=sQuery(id+"F0.wireOp",EDGE,"E9.0.7.1");
            var Q384;
            Q384=sQuery(id+"F0.wireOp",EDGE,"E9.0.12.2");
            var Q385;
            Q385=sQuery(id+"F0.wireOp",EDGE,"E9.0.18.0");
            var Q386;
            Q386=sQuery(id+"F0.wireOp",EDGE,"E9.0.12.1");
            var Q387;
            Q387=sQuery(id+"F0.wireOp",EDGE,"E9.0.17.2");
            var Q388;
            Q388=sQuery(id+"F0.wireOp",EDGE,"E11.17.0.2");
            var Q389;
            Q389=sQuery(id+"F0.wireOp",EDGE,"E9.0.16.1");
            var Q390;
            Q390=sQuery(id+"F0.wireOp",EDGE,"E9.0.11.0");
            var Q391;
            Q391=sQuery(id+"F0.wireOp",EDGE,"E9.0.5.2");
            var Q392;
            Q392=sQuery(id+"F0.wireOp",EDGE,"E9.0.16.2");
            var Q393;
            Q393=sQuery(id+"F0.wireOp",EDGE,"E9.0.11.1");
            var Q394;
            Q394=sQuery(id+"F0.wireOp",EDGE,"E9.0.6.0");
            var Q395;
            Q395=sQuery(id+"F0.wireOp",EDGE,"E11.26.0.0");
            var Q396;
            Q396=sQuery(id+"F0.wireOp",EDGE,"E9.0.17.0");
            var Q397;
            Q397=sQuery(id+"F0.wireOp",EDGE,"E9.0.6.1");
            var Q398;
            Q398=sQuery(id+"F0.wireOp",EDGE,"E11.18.0.1");
            var Q399;
            Q399=sQuery(id+"F0.wireOp",EDGE,"E9.0.16.0");
            var Q400;
            Q400=sQuery(id+"F0.wireOp",EDGE,"E11.40.0.3");
            var Q401;
            Q401=sQuery(id+"F0.wireOp",EDGE,"E11.29.0.0");
            var Q402;
            Q402=sQuery(id+"F0.wireOp",EDGE,"E11.28.0.3");
            var Q403;
            Q403=sQuery(id+"F0.wireOp",EDGE,"E11.4.0.3");
            var Q404;
            Q404=sQuery(id+"F0.wireOp",EDGE,"E11.8.0.3");
            var Q405;
            Q405=sQuery(id+"F0.wireOp",EDGE,"E11.13.0.1");
            var Q406;
            Q406=sQuery(id+"F0.wireOp",EDGE,"E11.17.0.1");
            var Q407;
            Q407=sQuery(id+"F0.wireOp",EDGE,"E11.5.0.0");
            var Q408;
            Q408=sQuery(id+"F0.wireOp",EDGE,"E11.9.0.0");
            var Q409;
            Q409=sQuery(id+"F0.wireOp",EDGE,"E11.40.0.2");
            var Q410;
            Q410=sQuery(id+"F0.wireOp",EDGE,"E11.32.0.2");
            var Q411;
            Q411=sQuery(id+"F0.wireOp",EDGE,"E11.4.0.2");
            var Q412;
            Q412=sQuery(id+"F0.wireOp",EDGE,"E11.12.0.2");
            var Q413;
            Q413=sQuery(id+"F0.wireOp",EDGE,"E9.0.9.1");
            var Q414;
            Q414=sQuery(id+"F0.wireOp",EDGE,"E9.0.4.0");
            var Q415;
            Q415=sQuery(id+"F0.wireOp",EDGE,"E11.28.0.1");
            var Q416;
            Q416=sQuery(id+"F0.wireOp",EDGE,"E11.32.0.1");
            var Q417;
            Q417=sQuery(id+"F0.wireOp",EDGE,"E11.8.0.1");
            var Q418;
            Q418=sQuery(id+"F0.wireOp",EDGE,"E9.0.14.1");
            var Q419;
            Q419=sQuery(id+"F0.wireOp",EDGE,"E11.32.0.0");
            var Q420;
            Q420=sQuery(id+"F0.wireOp",EDGE,"E11.12.0.0");
            var Q421;
            Q421=sQuery(id+"F0.wireOp",EDGE,"E9.0.19.1");
            var Q422;
            Q422=sQuery(id+"F0.wireOp",EDGE,"E11.23.0.3");
            var Q423;
            Q423=sQuery(id+"F0.wireOp",EDGE,"E11.27.0.3");
            var Q424;
            Q424=sQuery(id+"F0.wireOp",EDGE,"E11.31.0.3");
            var Q425;
            Q425=sQuery(id+"F0.wireOp",EDGE,"E11.3.0.3");
            var Q426;
            Q426=sQuery(id+"F0.wireOp",EDGE,"E11.11.0.3");
            var Q427;
            Q427=sQuery(id+"F0.wireOp",EDGE,"E9.0.3.0");
            var Q428;
            Q428=sQuery(id+"F0.wireOp",EDGE,"E11.39.0.3");
            var Q429;
            Q429=sQuery(id+"F0.wireOp",EDGE,"E11.43.0.3");
            var Q430;
            Q430=sQuery(id+"F0.wireOp",EDGE,"E11.39.0.2");
            var Q431;
            Q431=sQuery(id+"F0.wireOp",EDGE,"E11.27.0.2");
            var Q432;
            Q432=sQuery(id+"F0.wireOp",EDGE,"E11.3.0.1");
            var Q433;
            Q433=sQuery(id+"F0.wireOp",EDGE,"E11.7.0.1");
            var Q434;
            Q434=sQuery(id+"F0.wireOp",EDGE,"E11.39.0.0");
            var Q435;
            Q435=sQuery(id+"F0.wireOp",EDGE,"E11.38.0.3");
            var Q436;
            Q436=sQuery(id+"F0.wireOp",EDGE,"E11.30.0.3");
            var Q437;
            Q437=sQuery(id+"F0.wireOp",EDGE,"E11.2.0.3");
            var Q438;
            Q438=sQuery(id+"F0.wireOp",EDGE,"E11.10.0.3");
            var Q439;
            Q439=sQuery(id+"F0.wireOp",EDGE,"E9.0.7.0");
            var Q440;
            Q440=sQuery(id+"F0.wireOp",EDGE,"E11.42.0.2");
            var Q441;
            Q441=sQuery(id+"F0.wireOp",EDGE,"E9.0.17.1");
            var Q442;
            Q442=sQuery(id+"F0.wireOp",EDGE,"E9.0.12.0");
            var Q443;
            Q443=sQuery(id+"F0.wireOp",EDGE,"E11.10.0.2");
            var Q444;
            Q444=sQuery(id+"F0.wireOp",EDGE,"E11.22.0.2");
            var Q445;
            Q445=sQuery(id+"F0.wireOp",EDGE,"E11.30.0.2");
            var Q446;
            Q446=sQuery(id+"F0.wireOp",EDGE,"E11.9.0.2");
            var Q447;
            Q447=sQuery(id+"F0.wireOp",EDGE,"E11.5.0.2");
            var Q448;
            Q448=sQuery(id+"F0.wireOp",EDGE,"E11.41.0.2");
            var Q449;
            Q449=sQuery(id+"F0.wireOp",EDGE,"E11.37.0.2");
            var Q450;
            Q450=sQuery(id+"F0.wireOp",EDGE,"E11.29.0.2");
            var Q451;
            Q451=sQuery(id+"F0.wireOp",EDGE,"E11.9.0.3");
            var Q452;
            Q452=sQuery(id+"F0.wireOp",EDGE,"E11.5.0.3");
            var Q453;
            Q453=sQuery(id+"F0.wireOp",EDGE,"E11.21.0.3");
            var Q454;
            Q454=sQuery(id+"F0.wireOp",EDGE,"E11.13.0.3");
            var Q455;
            Q455=sQuery(id+"F0.wireOp",EDGE,"E11.41.0.3");
            var Q456;
            Q456=sQuery(id+"F0.wireOp",EDGE,"E11.37.0.3");
            var Q457;
            Q457=sQuery(id+"F0.wireOp",EDGE,"E11.33.0.3");
            var Q458;
            Q458=sQuery(id+"F0.wireOp",EDGE,"E11.29.0.3");
            var Q459;
            Q459=sQuery(id+"F0.wireOp",EDGE,"E11.6.0.0");
            var Q460;
            Q460=sQuery(id+"F0.wireOp",EDGE,"E11.2.0.0");
            var Q461;
            Q461=sQuery(id+"F0.wireOp",EDGE,"E11.22.0.0");
            var Q462;
            Q462=sQuery(id+"F0.wireOp",EDGE,"E11.42.0.0");
            var Q463;
            Q463=sQuery(id+"F0.wireOp",EDGE,"E11.30.0.0");
            var Q464;
            Q464=sQuery(id+"F0.wireOp",EDGE,"E11.10.0.1");
            var Q465;
            Q465=sQuery(id+"F0.wireOp",EDGE,"E11.6.0.1");
            var Q466;
            Q466=sQuery(id+"F0.wireOp",EDGE,"E11.42.0.1");
            var Q467;
            Q467=sQuery(id+"F0.wireOp",EDGE,"E11.38.0.1");
            var Q468;
            Q468=sQuery(id+"F0.wireOp",EDGE,"E11.30.0.1");
            var Q469;
            Q469=sQuery(id+"F0.wireOp",EDGE,"E11.24.0.3");
            var Q470;
            Q470=sQuery(id+"F0.wireOp",EDGE,"E11.37.0.1");
            var Q471;
            Q471=sQuery(id+"F0.wireOp",EDGE,"E11.25.0.0");
            var Q472;
            Q472=sQuery(id+"F0.wireOp",EDGE,"E11.25.0.1");
            var Q473;
            Q473=sQuery(id+"F0.wireOp",EDGE,"E11.9.0.1");
            var Q474;
            Q474=sQuery(id+"F0.wireOp",EDGE,"E11.24.0.2");
            var Q475;
            Q475=sQuery(id+"F0.wireOp",EDGE,"E11.28.0.2");
            var Q476;
            Q476=sQuery(id+"F0.wireOp",EDGE,"E11.4.0.1");
            var Q477;
            Q477=sQuery(id+"F0.wireOp",EDGE,"E9.0.9.0");
            var Q478;
            Q478=sQuery(id+"F0.wireOp",EDGE,"E11.40.0.0");
            var Q479;
            Q479=sQuery(id+"F0.wireOp",EDGE,"E11.28.0.0");
            var Q480;
            Q480=sQuery(id+"F0.wireOp",EDGE,"E11.8.0.0");
            var Q481;
            Q481=sQuery(id+"F0.wireOp",EDGE,"E9.0.14.0");
            var Q482;
            Q482=sQuery(id+"F0.wireOp",EDGE,"E11.11.0.2");
            var Q483;
            Q483=sQuery(id+"F0.wireOp",EDGE,"E11.43.0.2");
            var Q484;
            Q484=sQuery(id+"F0.wireOp",EDGE,"E11.23.0.2");
            var Q485;
            Q485=sQuery(id+"F0.wireOp",EDGE,"E11.31.0.2");
            var Q486;
            Q486=sQuery(id+"F0.wireOp",EDGE,"E11.39.0.1");
            var Q487;
            Q487=sQuery(id+"F0.wireOp",EDGE,"E11.27.0.1");
            var Q488;
            Q488=sQuery(id+"F0.wireOp",EDGE,"E11.26.0.3");
            var Q489;
            Q489=sQuery(id+"F0.wireOp",EDGE,"E11.6.0.3");
            var Q490;
            Q490=sQuery(id+"F0.wireOp",EDGE,"E11.38.0.2");
            var Q491;
            Q491=sQuery(id+"F0.wireOp",EDGE,"E11.2.0.2");
            var Q492;
            Q492=sQuery(id+"F0.wireOp",EDGE,"E9.0.21.1");
            var Q493;
            Q493=sQuery(id+"F0.wireOp",EDGE,"E11.25.0.2");
            var Q494;
            Q494=sQuery(id+"F0.wireOp",EDGE,"E11.21.0.2");
            var Q495;
            Q495=sQuery(id+"F0.wireOp",EDGE,"E11.33.0.2");
            var Q496;
            Q496=sQuery(id+"F0.wireOp",EDGE,"E9.0.21.2");
            var Q497;
            Q497=sQuery(id+"F0.wireOp",EDGE,"E11.25.0.3");
            var Q498;
            Q498=sQuery(id+"F0.wireOp",EDGE,"E11.36.0.3");
            var Q499;
            Q499=sQuery(id+"F0.wireOp",EDGE,"E11.33.0.0");
            var Q500;
            Q500=sQuery(id+"F0.wireOp",EDGE,"E11.20.0.3");
            var Q501;
            Q501=sQuery(id+"F0.wireOp",EDGE,"E11.21.0.0");
            var Q502;
            Q502=sQuery(id+"F0.wireOp",EDGE,"E11.16.0.3");
            var Q503;
            Q503=sQuery(id+"F0.wireOp",EDGE,"E9.0.21.0");
            var Q504;
            Q504=sQuery(id+"F0.wireOp",EDGE,"E11.20.0.2");
            var Q505;
            Q505=sQuery(id+"F0.wireOp",EDGE,"E11.20.0.1");
            var Q506;
            Q506=sQuery(id+"F0.wireOp",EDGE,"E11.24.0.1");
            var Q507;
            Q507=sQuery(id+"F0.wireOp",EDGE,"E11.4.0.0");
            var Q508;
            Q508=sQuery(id+"F0.wireOp",EDGE,"E11.19.0.3");
            var Q509;
            Q509=sQuery(id+"F0.wireOp",EDGE,"E11.15.0.3");
            var Q510;
            Q510=sQuery(id+"F0.wireOp",EDGE,"E11.35.0.3");
            var Q511;
            Q511=sQuery(id+"F0.wireOp",EDGE,"E11.15.0.2");
            var Q512;
            Q512=sQuery(id+"F0.wireOp",EDGE,"E11.35.0.2");
            var Q513;
            Q513=sQuery(id+"F0.wireOp",EDGE,"E11.19.0.2");
            var Q514;
            Q514=sQuery(id+"F0.wireOp",EDGE,"E11.35.0.1");
            var Q515;
            Q515=sQuery(id+"F0.wireOp",EDGE,"E11.11.0.1");
            var Q516;
            Q516=sQuery(id+"F0.wireOp",EDGE,"E11.23.0.0");
            var Q517;
            Q517=sQuery(id+"F0.wireOp",EDGE,"E11.19.0.0");
            var Q518;
            Q518=sQuery(id+"F0.wireOp",EDGE,"E11.15.0.0");
            var Q519;
            Q519=sQuery(id+"F0.wireOp",EDGE,"E11.18.0.3");
            var Q520;
            Q520=sQuery(id+"F0.wireOp",EDGE,"E11.34.0.2");
            var Q521;
            Q521=sQuery(id+"F0.wireOp",EDGE,"E11.14.0.2");
            var Q522;
            Q522=sQuery(id+"F0.wireOp",EDGE,"E11.26.0.2");
            var Q523;
            Q523=sQuery(id+"F0.wireOp",EDGE,"E11.6.0.2");
            var Q524;
            Q524=sQuery(id+"F0.wireOp",EDGE,"E11.18.0.0");
            var Q525;
            Q525=sQuery(id+"F0.wireOp",EDGE,"E11.14.0.1");
            var Q526;
            Q526=sQuery(id+"F0.wireOp",EDGE,"E11.34.0.1");
            var Q527;
            Q527=sQuery(id+"F0.wireOp",EDGE,"E11.36.0.2");
            var Q528;
            Q528=sQuery(id+"F0.wireOp",EDGE,"E11.16.0.2");
            var Q529;
            Q529=sQuery(id+"F0.wireOp",EDGE,"E11.16.0.1");
            var Q530;
            Q530=sQuery(id+"F0.wireOp",EDGE,"E11.35.0.0");
            var Q531;
            Q531=sQuery(id+"F0.wireOp",EDGE,"E11.11.0.0");
            var Q532;
            Q532=sQuery(id+"F0.wireOp",EDGE,"E11.34.0.3");
            var Q533;
            Q533=sQuery(id+"F0.wireOp",EDGE,"E11.14.0.3");
            var Q534;
            Q534=sQuery(id+"F0.wireOp",EDGE,"E11.16.0.0");
            var Q535;
            Q535=sQuery(id+"F0.wireOp",EDGE,"E10.right");
            var Q536;
            Q536=sQuery(id+"F0.wireOp",EDGE,"E10.left");
            var Q537;
            Q537=sQuery(id+"F0.wireOp",EDGE,"E10.top");
            var Q538;
            Q538=sQuery(id+"F0.wireOp",EDGE,"E10.bottom");
            var Q539;
            Q539=sQuery(id+"F0.wireOp",EDGE,"E9.0.2.1");
            var Q540;
            Q540=sQuery(id+"F0.wireOp",EDGE,"E9.0.23.1");
            var Q541;
            Q541=sQuery(id+"F0.wireOp",EDGE,"E9.0.22.2");
            var Q542;
            Q542=sQuery(id+"F0.wireOp",EDGE,"E11.1.0.3");
            var Q543;
            Q543=sQuery(id+"F0.wireOp",EDGE,"E9.0.22.1");
            var Q544;
            Q544=sQuery(id+"F0.wireOp",EDGE,"E9.0.2.0");
            var Q545;
            Q545=sQuery(id+"F0.wireOp",EDGE,"E8.bottom");
            var Q546;
            Q546=sQuery(id+"F0.wireOp",EDGE,"E8.top");
            var Q547;
            Q547=sQuery(id+"F0.wireOp",EDGE,"E8.right");
            var Q548;
            Q548=sQuery(id+"F0.wireOp",EDGE,"E9.0.1.0");
            var Q549;
            Q549=sQuery(id+"F0.wireOp",EDGE,"E11.1.0.2");
            var Q550;
            Q550=sQuery(id+"F0.wireOp",EDGE,"E9.0.22.0");
            var Q551;
            Q551=sQuery(id+"F0.wireOp",EDGE,"E9.0.1.1");
            var Q552;
            Q552=sQuery(id+"F0.wireOp",EDGE,"E11.1.0.0");
            var Q553;
            Q553=sQuery(id+"F0.wireOp",EDGE,"E9.0.23.2");
            var Q554;
            Q554=sQuery(id+"F0.wireOp",EDGE,"E9.0.23.0");
            var Q555;
            Q555=sQuery(id+"F0.wireOp",EDGE,"E9.0.20.2");
            var Q556;
            Q556=sQuery(id+"F0.wireOp",EDGE,"E9.0.4.2");
            var Q557;
            Q557=sQuery(id+"F0.wireOp",EDGE,"E9.0.20.0");
            var Q558;
            Q558=sQuery(id+"F0.wireOp",EDGE,"E9.0.8.2");
            var Q559;
            Q559=sQuery(id+"F0.wireOp",EDGE,"E9.0.13.2");
            var Q560;
            Q560=sQuery(id+"F0.wireOp",EDGE,"E9.0.6.2");
            var Q561;
            Q561=sQuery(id+"F0.wireOp",EDGE,"E9.0.11.2");
            var Q562;
            Q562=sQuery(id+"F0.wireOp",EDGE,"E11.3.0.2");
            var Q563;
            Q563=sQuery(id+"F0.wireOp",EDGE,"E9.0.18.2");
            var Q564;
            Q564=sQuery(id+"F0.wireOp",EDGE,"E11.5.0.1");
            var Q565;
            Q565=sQuery(id+"F0.wireOp",EDGE,"E11.3.0.0");
            var Q566;
            Q566=sQuery(id+"F0.wireOp",EDGE,"E11.2.0.1");
            var Q567;
            Q567=sQuery(id+"F0.wireOp",EDGE,"E11.1.0.1");
            var Q568;
            Q568=sQuery(id+"F0.wireOp",EDGE,"E9.0.1.2");
            var Q569;
            Q569=sQuery(id+"F0.wireOp",EDGE,"E8.left");
            extrude(context, id + "F1", {"entities" : qUnion([Q0, Q1, Q2, Q3, Q4, Q5, Q6, Q7, Q8, Q9, Q10, Q11, Q12, Q13, Q14, Q15, Q16, Q17, Q18, Q19, Q20, Q21, Q22, Q23, Q24, Q25, Q26, Q27, Q28, Q29, Q30, Q31, Q32, Q33, Q34, Q35, Q36, Q37, Q38, Q39, Q40, Q41, Q42, Q43, Q44, Q45, Q46, Q47, Q48, Q49, Q50, Q51, Q52, Q53, Q54, Q55, Q56, Q57, Q58, Q59, Q60, Q61, Q62, Q63, Q64, Q65, Q66, Q67, Q68, Q69, Q70, Q71, Q72, Q73, Q74, Q75, Q76, Q77, Q78, Q79, Q80, Q81, Q82, Q83, Q84, Q85, Q86, Q87, Q88, Q89, Q90, Q91, Q92, Q93, Q94, Q95, Q96, Q97, Q98, Q99, Q100, Q101, Q102, Q103, Q104, Q105, Q106, Q107, Q108, Q109, Q110, Q111, Q112, Q113, Q114, Q115, Q116, Q117, Q118, Q119, Q120, Q121, Q122, Q123, Q124]), "surfaceEntities" : qUnion([Q125, Q126, Q127, Q128, Q129, Q130, Q131, Q132, Q133, Q134, Q135, Q136, Q137, Q138, Q139, Q140, Q141, Q142, Q143, Q144, Q145, Q146, Q147, Q148, Q149, Q150, Q151, Q152, Q153, Q154, Q155, Q156, Q157, Q158, Q159, Q160, Q161, Q162, Q163, Q164, Q165, Q166, Q167, Q168, Q169, Q170, Q171, Q172, Q173, Q174, Q175, Q176, Q177, Q178, Q179, Q180, Q181, Q182, Q183, Q184, Q185, Q186, Q187, Q188, Q189, Q190, Q191, Q192, Q193, Q194, Q195, Q196, Q197, Q198, Q199, Q200, Q201, Q202, Q203, Q204, Q205, Q206, Q207, Q208, Q209, Q210, Q211, Q212, Q213, Q214, Q215, Q216, Q217, Q218, Q219, Q220, Q221, Q222, Q223, Q224, Q225, Q226, Q227, Q228, Q229, Q230, Q231, Q232, Q233, Q234, Q235, Q236, Q237, Q238, Q239, Q240, Q241, Q242, Q243, Q244, Q245, Q246, Q247, Q248, Q249, Q250, Q251, Q252, Q253, Q254, Q255, Q256, Q257, Q258, Q259, Q260, Q261, Q262, Q263, Q264, Q265, Q266, Q267, Q268, Q269, Q270, Q271, Q272, Q273, Q274, Q275, Q276, Q277, Q278, Q279, Q280, Q281, Q282, Q283, Q284, Q285, Q286, Q287, Q288, Q289, Q290, Q291, Q292, Q293, Q294, Q295, Q296, Q297, Q298, Q299, Q300, Q301, Q302, Q303, Q304, Q305, Q306, Q307, Q308, Q309, Q310, Q311, Q312, Q313, Q314, Q315, Q316, Q317, Q318, Q319, Q320, Q321, Q322, Q323, Q324, Q325, Q326, Q327, Q328, Q329, Q330, Q331, Q332, Q333, Q334, Q335, Q336, Q337, Q338, Q339, Q340, Q341, Q342, Q343, Q344, Q345, Q346, Q347, Q348, Q349, Q350, Q351, Q352, Q353, Q354, Q355, Q356, Q357, Q358, Q359, Q360, Q361, Q362, Q363, Q364, Q365, Q366, Q367, Q368, Q369, Q370, Q371, Q372, Q373, Q374, Q375, Q376, Q377, Q378, Q379, Q380, Q381, Q382, Q383, Q384, Q385, Q386, Q387, Q388, Q389, Q390, Q391, Q392, Q393, Q394, Q395, Q396, Q397, Q398, Q399, Q400, Q401, Q402, Q403, Q404, Q405, Q406, Q407, Q408, Q409, Q410, Q411, Q412, Q413, Q414, Q415, Q416, Q417, Q418, Q419, Q420, Q421, Q422, Q423, Q424, Q425, Q426, Q427, Q428, Q429, Q430, Q431, Q432, Q433, Q434, Q435, Q436, Q437, Q438, Q439, Q440, Q441, Q442, Q443, Q444, Q445, Q446, Q447, Q448, Q449, Q450, Q451, Q452, Q453, Q454, Q455, Q456, Q457, Q458, Q459, Q460, Q461, Q462, Q463, Q464, Q465, Q466, Q467, Q468, Q469, Q470, Q471, Q472, Q473, Q474, Q475, Q476, Q477, Q478, Q479, Q480, Q481, Q482, Q483, Q484, Q485, Q486, Q487, Q488, Q489, Q490, Q491, Q492, Q493, Q494, Q495, Q496, Q497, Q498, Q499, Q500, Q501, Q502, Q503, Q504, Q505, Q506, Q507, Q508, Q509, Q510, Q511, Q512, Q513, Q514, Q515, Q516, Q517, Q518, Q519, Q520, Q521, Q522, Q523, Q524, Q525, Q526, Q527, Q528, Q529, Q530, Q531, Q532, Q533, Q534, Q535, Q536, Q537, Q538, Q539, Q540, Q541, Q542, Q543, Q544, Q545, Q546, Q547, Q548, Q549, Q550, Q551, Q552, Q553, Q554, Q555, Q556, Q557, Q558, Q559, Q560, Q561, Q562, Q563, Q564, Q565, Q566, Q567, Q568, Q569]), "depth" : 1066.8 * mm});
        }
        {
            var Q0;
            Q0 = qSketchRegion(id + "F0", true);
            extrude(context, id + "F2", {"entities" : qUnion([Q0]), "operationType" : NewBodyOperationType.ADD, "depth" : 38.1 * mm});
        }
    });
